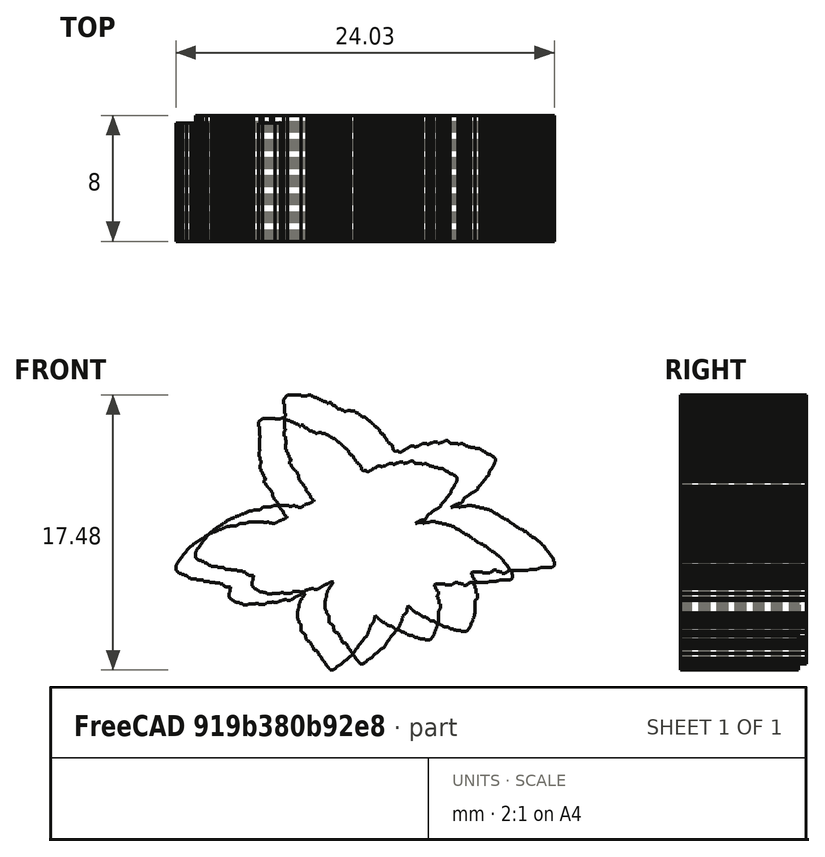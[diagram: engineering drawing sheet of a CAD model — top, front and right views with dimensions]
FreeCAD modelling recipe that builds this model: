
FCSTD DOCUMENT  (FreeCAD 1.0R39285 (Git))
Label: mintsLeafLogo_01_13_2023
License: All rights reserved
LicenseURL: http://en.wikipedia.org/wiki/All_rights_reserved
objects: Part::FeaturePython×2, Sketcher::SketchObject×1, Mesh::Feature×1, Part::Extrusion×1
note: 5 computed .brp shape members not serialized (recipe doc carries the construction recipe); baked Part::Feature solids carry a one-line shape summary decoded from their .brp

FEATURE [Sketcher::SketchObject] Sketch013
  ArcFitTolerance = 0
  FullyConstrained = false
  MakeInternals = false
  Placement = pos=(0,0,0) rot=(1,0,0;1.5708rad)
  sketch-geometry (884):
    g0: LineSegment StartX=35.7189 StartY=14.4677 StartZ=0 EndX=35.5415 EndY=14.2824 EndZ=0
    g1: LineSegment StartX=35.5415 StartY=14.2079 StartZ=0 EndX=35.4533 EndY=14.1342 EndZ=0
    g2: LineSegment StartX=35.4533 StartY=14.1342 StartZ=0 EndX=35.4583 EndY=14.0618 EndZ=0
    g3: LineSegment StartX=35.4583 StartY=14.0618 StartZ=0 EndX=35.3195 EndY=13.9216 EndZ=0
    g4: LineSegment StartX=35.3195 StartY=13.9216 StartZ=0 EndX=35.3195 EndY=13.853 EndZ=0
    g5: LineSegment StartX=35.3195 StartY=13.853 StartZ=0 EndX=35.248 EndY=13.7975 EndZ=0
    g6: LineSegment StartX=35.248 StartY=13.7975 StartZ=0 EndX=35.248 EndY=13.6573 EndZ=0
    g7: LineSegment StartX=35.248 StartY=13.6573 StartZ=0 EndX=35.1825 EndY=13.5912 EndZ=0
    g8: LineSegment StartX=35.1825 StartY=13.5912 StartZ=0 EndX=35.1825 EndY=13.2647 EndZ=0
    g9: LineSegment StartX=35.1825 StartY=13.2647 StartZ=0 EndX=35.0994 EndY=13.159 EndZ=0
    g10: LineSegment StartX=35.0994 StartY=13.159 StartZ=0 EndX=35.0994 EndY=13.0459 EndZ=0
    g11: LineSegment StartX=35.0994 StartY=13.0459 StartZ=0 EndX=35.0336 EndY=12.9565 EndZ=0
    g12: LineSegment StartX=35.0336 StartY=12.9565 StartZ=0 EndX=35.0336 EndY=12.3489 EndZ=0
    g13: LineSegment StartX=35.0336 StartY=12.3489 StartZ=0 EndX=35.1008 EndY=12.3489 EndZ=0
    g14: LineSegment StartX=35.1008 StartY=12.3489 StartZ=0 EndX=35.1008 EndY=12.2102 EndZ=0
    g15: LineSegment StartX=35.1008 StartY=12.2102 StartZ=0 EndX=35.1709 EndY=12.2072 EndZ=0
    g16: LineSegment StartX=35.1709 StartY=12.2072 StartZ=0 EndX=35.1709 EndY=11.9948 EndZ=0
    g17: LineSegment StartX=35.1709 StartY=11.9948 StartZ=0 EndX=35.2359 EndY=11.9948 EndZ=0
    g18: LineSegment StartX=35.2359 StartY=11.9948 StartZ=0 EndX=35.2359 EndY=11.9181 EndZ=0
    g19: LineSegment StartX=35.2359 StartY=11.9181 StartZ=0 EndX=35.3001 EndY=11.9181 EndZ=0
    g20: LineSegment StartX=35.3001 StartY=11.9181 StartZ=0 EndX=35.3001 EndY=11.8402 EndZ=0
    g21: LineSegment StartX=35.3001 StartY=11.8402 StartZ=0 EndX=35.3675 EndY=11.8402 EndZ=0
    g22: LineSegment StartX=35.3675 StartY=11.8402 StartZ=0 EndX=35.3675 EndY=11.2433 EndZ=0
    g23: LineSegment StartX=35.3675 StartY=11.2433 StartZ=0 EndX=35.435 EndY=11.2433 EndZ=0
    g24: LineSegment StartX=35.435 StartY=11.2433 StartZ=0 EndX=35.435 EndY=11.1727 EndZ=0
    g25: LineSegment StartX=35.435 StartY=11.1727 StartZ=0 EndX=35.5098 EndY=11.1727 EndZ=0
    g26: LineSegment StartX=35.5098 StartY=11.1727 StartZ=0 EndX=35.5098 EndY=11.1026 EndZ=0
    g27: LineSegment StartX=35.5098 StartY=11.1026 StartZ=0 EndX=35.6558 EndY=11.1026 EndZ=0
    g28: LineSegment StartX=35.6558 StartY=11.1026 StartZ=0 EndX=35.6558 EndY=11.0252 EndZ=0
    g29: LineSegment StartX=35.6558 StartY=11.0252 StartZ=0 EndX=35.7128 EndY=11.0252 EndZ=0
    g30: LineSegment StartX=35.7128 StartY=11.0252 StartZ=0 EndX=35.7128 EndY=10.7682 EndZ=0
    g31: LineSegment StartX=35.7128 StartY=10.7682 StartZ=0 EndX=35.7756 EndY=10.7681 EndZ=0
    g32: LineSegment StartX=35.7756 StartY=10.7681 StartZ=0 EndX=35.7756 EndY=10.5644 EndZ=0
    g33: LineSegment StartX=35.7756 StartY=10.5644 StartZ=0 EndX=35.846 EndY=10.5644 EndZ=0
    g34: LineSegment StartX=35.846 StartY=10.5644 StartZ=0 EndX=35.846 EndY=10.4767 EndZ=0
    g35: LineSegment StartX=35.846 StartY=10.4767 StartZ=0 EndX=35.988 EndY=10.4767 EndZ=0
    g36: LineSegment StartX=35.988 StartY=10.4767 StartZ=0 EndX=35.988 EndY=10.4228 EndZ=0
    g37: LineSegment StartX=35.988 StartY=10.4228 StartZ=0 EndX=36.1201 EndY=10.4228 EndZ=0
    g38: LineSegment StartX=36.1201 StartY=10.4228 StartZ=0 EndX=36.1201 EndY=10.2907 EndZ=0
    g39: LineSegment StartX=36.1201 StartY=10.2907 StartZ=0 EndX=36.1926 EndY=10.2907 EndZ=0
    g40: LineSegment StartX=36.1926 StartY=10.2907 StartZ=0 EndX=36.1926 EndY=10.1585 EndZ=0
    g41: LineSegment StartX=36.1926 StartY=10.1585 StartZ=0 EndX=36.2533 EndY=10.1585 EndZ=0
    g42: LineSegment StartX=36.2533 StartY=10.1585 StartZ=0 EndX=36.2533 EndY=10.0897 EndZ=0
    g43: LineSegment StartX=36.2533 StartY=10.0897 StartZ=0 EndX=36.3179 EndY=10.0897 EndZ=0
    g44: LineSegment StartX=36.3179 StartY=10.0897 StartZ=0 EndX=36.3179 EndY=9.8871 EndZ=0
    g45: LineSegment StartX=36.3179 StartY=9.8871 StartZ=0 EndX=36.3888 EndY=9.8871 EndZ=0
    g46: LineSegment StartX=36.3888 StartY=9.8871 StartZ=0 EndX=36.3888 EndY=9.73503 EndZ=0
    g47: LineSegment StartX=36.3888 StartY=9.73503 StartZ=0 EndX=36.4516 EndY=9.73503 EndZ=0
    g48: LineSegment StartX=36.4516 StartY=9.73503 StartZ=0 EndX=36.4516 EndY=9.65617 EndZ=0
    g49: LineSegment StartX=36.4516 StartY=9.65617 StartZ=0 EndX=36.6707 EndY=9.65617 EndZ=0
    g50: LineSegment StartX=36.6707 StartY=9.65617 StartZ=0 EndX=36.6707 EndY=9.58899 EndZ=0
    g51: LineSegment StartX=36.6707 StartY=9.58899 StartZ=0 EndX=36.7335 EndY=9.58899 EndZ=0
    g52: LineSegment StartX=36.7335 StartY=9.58899 StartZ=0 EndX=36.7335 EndY=9.51158 EndZ=0
    g53: LineSegment StartX=36.7335 StartY=9.51158 StartZ=0 EndX=36.7948 EndY=9.51158 EndZ=0
    g54: LineSegment StartX=36.7948 StartY=9.51158 StartZ=0 EndX=36.7948 EndY=9.40351 EndZ=0
    g55: LineSegment StartX=36.7948 StartY=9.40351 StartZ=0 EndX=36.8664 EndY=9.40351 EndZ=0
    g56: LineSegment StartX=36.8664 StartY=9.40351 StartZ=0 EndX=36.8664 EndY=9.2487 EndZ=0
    g57: LineSegment StartX=36.8664 StartY=9.2487 StartZ=0 EndX=36.9292 EndY=9.2487 EndZ=0
    g58: LineSegment StartX=36.9292 StartY=9.2487 StartZ=0 EndX=36.9292 EndY=9.18298 EndZ=0
    g59: LineSegment StartX=36.9292 StartY=9.18298 StartZ=0 EndX=37.0036 EndY=9.18298 EndZ=0
    g60: LineSegment StartX=37.0036 StartY=9.18298 StartZ=0 EndX=37.0036 EndY=9.12121 EndZ=0
    g61: LineSegment StartX=37.0036 StartY=9.12121 StartZ=0 EndX=37.066 EndY=9.12121 EndZ=0
    g62: LineSegment StartX=37.066 StartY=9.12121 StartZ=0 EndX=37.066 EndY=8.98122 EndZ=0
    g63: LineSegment StartX=37.066 StartY=8.98122 StartZ=0 EndX=37.1365 EndY=8.98122 EndZ=0
    g64: LineSegment StartX=37.1365 StartY=8.98122 StartZ=0 EndX=37.1365 EndY=8.85617 EndZ=0
    g65: LineSegment StartX=37.1365 StartY=8.85617 StartZ=0 EndX=37.2117 EndY=8.85617 EndZ=0
    g66: LineSegment StartX=37.2117 StartY=8.85617 StartZ=0 EndX=37.2117 EndY=8.77808 EndZ=0
    g67: LineSegment StartX=37.2117 StartY=8.77808 StartZ=0 EndX=37.276 EndY=8.7779 EndZ=0
    g68: LineSegment StartX=37.276 StartY=8.7779 StartZ=0 EndX=37.276 EndY=8.70839 EndZ=0
    g69: LineSegment StartX=37.276 StartY=8.70839 StartZ=0 EndX=37.3475 EndY=8.70839 EndZ=0
    g70: LineSegment StartX=37.3475 StartY=8.70839 StartZ=0 EndX=37.3475 EndY=8.58602 EndZ=0
    g71: LineSegment StartX=37.3475 StartY=8.58602 StartZ=0 EndX=37.4111 EndY=8.58602 EndZ=0
    g72: LineSegment StartX=37.4111 StartY=8.58602 StartZ=0 EndX=37.4111 EndY=8.50272 EndZ=0
    g73: LineSegment StartX=37.4111 StartY=8.50272 StartZ=0 EndX=37.4778 EndY=8.50272 EndZ=0
    g74: LineSegment StartX=37.4778 StartY=8.50272 StartZ=0 EndX=37.4778 EndY=8.37852 EndZ=0
    g75: LineSegment StartX=37.4778 StartY=8.37852 StartZ=0 EndX=37.55 EndY=8.37852 EndZ=0
    g76: LineSegment StartX=37.55 StartY=8.37852 StartZ=0 EndX=37.55 EndY=8.29594 EndZ=0
    g77: LineSegment StartX=37.55 StartY=8.29594 StartZ=0 EndX=37.6238 EndY=8.29594 EndZ=0
    g78: LineSegment StartX=37.6238 StartY=8.29594 StartZ=0 EndX=37.6238 EndY=8.20831 EndZ=0
    g79: LineSegment StartX=37.6238 StartY=8.20831 StartZ=0 EndX=37.6953 EndY=8.21123 EndZ=0
    g80: LineSegment StartX=37.6953 StartY=8.21123 StartZ=0 EndX=37.6953 EndY=8.14022 EndZ=0
    g81: LineSegment StartX=37.6953 StartY=8.14022 StartZ=0 EndX=37.7536 EndY=8.14414 EndZ=0
    g82: LineSegment StartX=37.7536 StartY=8.14414 StartZ=0 EndX=37.7574 EndY=8.06459 EndZ=0
    g83: LineSegment StartX=37.7574 StartY=8.06459 StartZ=0 EndX=37.8181 EndY=8.06459 EndZ=0
    g84: LineSegment StartX=37.8181 StartY=8.06459 StartZ=0 EndX=37.8216 EndY=7.98967 EndZ=0
    g85: LineSegment StartX=37.8216 StartY=7.98967 StartZ=0 EndX=38.1025 EndY=7.98967 EndZ=0
    g86: LineSegment StartX=38.1025 StartY=7.98967 StartZ=0 EndX=38.1917 EndY=8.08042 EndZ=0
    g87: LineSegment StartX=38.1917 StartY=8.08042 StartZ=0 EndX=38.2417 EndY=8.08577 EndZ=0
    g88: LineSegment StartX=38.2417 StartY=8.08577 StartZ=0 EndX=38.4557 EndY=8.32302 EndZ=0
    g89: LineSegment StartX=38.4557 StartY=8.32302 StartZ=0 EndX=38.5235 EndY=8.32302 EndZ=0
    g90: LineSegment StartX=38.5235 StartY=8.32302 StartZ=0 EndX=38.5887 EndY=8.40314 EndZ=0
    g91: LineSegment StartX=38.5887 StartY=8.40314 StartZ=0 EndX=38.6773 EndY=8.40314 EndZ=0
    g92: LineSegment StartX=38.6773 StartY=8.40314 StartZ=0 EndX=39.0643 EndY=8.80818 EndZ=0
    g93: LineSegment StartX=39.0643 StartY=8.80818 StartZ=0 EndX=39.152 EndY=8.80818 EndZ=0
    g94: LineSegment StartX=39.152 StartY=8.80818 StartZ=0 EndX=39.5355 EndY=9.19803 EndZ=0
    g95: LineSegment StartX=39.5355 StartY=9.19803 StartZ=0 EndX=39.6318 EndY=9.19803 EndZ=0
    g96: LineSegment StartX=39.6318 StartY=9.19803 StartZ=0 EndX=39.792 EndY=9.38195 EndZ=0
    g97: LineSegment StartX=39.792 StartY=9.38195 StartZ=0 EndX=39.7884 EndY=9.45608 EndZ=0
    g98: LineSegment StartX=39.7884 StartY=9.45608 StartZ=0 EndX=39.9772 EndY=9.63446 EndZ=0
    g99: LineSegment StartX=39.9772 StartY=9.63446 StartZ=0 EndX=39.9772 EndY=9.72533 EndZ=0
    g100: LineSegment StartX=39.9772 StartY=9.72533 StartZ=0 EndX=40.1697 EndY=9.91904 EndZ=0
    g101: LineSegment StartX=40.1697 StartY=9.91904 StartZ=0 EndX=40.1746 EndY=9.99558 EndZ=0
    g102: LineSegment StartX=40.1746 StartY=9.99558 StartZ=0 EndX=40.2388 EndY=10.0603 EndZ=0
    g103: LineSegment StartX=40.2388 StartY=10.0603 StartZ=0 EndX=40.2423 EndY=10.1261 EndZ=0
    g104: LineSegment StartX=40.2423 StartY=10.1261 StartZ=0 EndX=40.5948 EndY=10.4793 EndZ=0
    g105: LineSegment StartX=40.5948 StartY=10.4793 StartZ=0 EndX=40.5948 EndY=10.5499 EndZ=0
    g106: LineSegment StartX=40.5948 StartY=10.5499 StartZ=0 EndX=40.6701 EndY=10.618 EndZ=0
    g107: LineSegment StartX=40.6701 StartY=10.618 StartZ=0 EndX=40.6581 EndY=10.6527 EndZ=0
    g108: LineSegment StartX=40.6581 StartY=10.6527 StartZ=0 EndX=40.6988 EndY=10.6527 EndZ=0
    g109: LineSegment StartX=40.6988 StartY=10.6527 StartZ=0 EndX=40.9317 EndY=10.8877 EndZ=0
    g110: LineSegment StartX=40.9317 StartY=10.8877 StartZ=0 EndX=40.9317 EndY=10.9592 EndZ=0
    g111: LineSegment StartX=40.9317 StartY=10.9592 StartZ=0 EndX=41.0136 EndY=11.0405 EndZ=0
    g112: LineSegment StartX=41.0136 StartY=11.0405 StartZ=0 EndX=41.0068 EndY=11.1648 EndZ=0
    g113: LineSegment StartX=41.0068 StartY=11.1648 StartZ=0 EndX=41.0763 EndY=11.2275 EndZ=0
    g114: LineSegment StartX=41.0763 StartY=11.2275 StartZ=0 EndX=41.0723 EndY=11.2979 EndZ=0
    g115: LineSegment StartX=41.0723 StartY=11.2979 StartZ=0 EndX=41.15 EndY=11.3821 EndZ=0
    g116: LineSegment StartX=41.15 StartY=11.3821 StartZ=0 EndX=41.15 EndY=11.5724 EndZ=0
    g117: LineSegment StartX=41.15 StartY=11.5724 StartZ=0 EndX=41.2317 EndY=11.6351 EndZ=0
    g118: LineSegment StartX=41.2317 StartY=11.6351 StartZ=0 EndX=41.2155 EndY=11.7717 EndZ=0
    g119: LineSegment StartX=41.2155 StartY=11.7717 StartZ=0 EndX=41.2837 EndY=11.8432 EndZ=0
    g120: LineSegment StartX=41.2837 StartY=11.8432 StartZ=0 EndX=41.2786 EndY=11.8698 EndZ=0
    g121: LineSegment StartX=41.2786 StartY=11.8698 StartZ=0 EndX=41.3138 EndY=11.8698 EndZ=0
    g122: LineSegment StartX=41.3138 StartY=11.8698 StartZ=0 EndX=41.5455 EndY=12.1045 EndZ=0
    g123: LineSegment StartX=41.5455 StartY=12.1045 StartZ=0 EndX=41.5618 EndY=12.4305 EndZ=0
    g124: LineSegment StartX=41.5618 StartY=12.4305 StartZ=0 EndX=41.6277 EndY=12.505 EndZ=0
    g125: LineSegment StartX=41.6277 StartY=12.505 StartZ=0 EndX=41.6277 EndY=12.6108 EndZ=0
    g126: LineSegment StartX=41.6277 StartY=12.6108 StartZ=0 EndX=41.692 EndY=12.5393 EndZ=0
    g127: LineSegment StartX=41.692 StartY=12.5393 StartZ=0 EndX=41.7679 EndY=12.5393 EndZ=0
    g128: LineSegment StartX=41.7679 StartY=12.5393 StartZ=0 EndX=41.7679 EndY=12.4516 EndZ=0
    g129: LineSegment StartX=41.7679 StartY=12.4516 StartZ=0 EndX=41.8336 EndY=12.4546 EndZ=0
    g130: LineSegment StartX=41.8336 StartY=12.4546 StartZ=0 EndX=41.8336 EndY=12.3903 EndZ=0
    g131: LineSegment StartX=41.8336 StartY=12.3903 StartZ=0 EndX=41.8935 EndY=12.3903 EndZ=0
    g132: LineSegment StartX=41.8935 StartY=12.3903 StartZ=0 EndX=41.8935 EndY=12.3173 EndZ=0
    g133: LineSegment StartX=41.8935 StartY=12.3173 StartZ=0 EndX=41.9592 EndY=12.3217 EndZ=0
    g134: LineSegment StartX=41.9592 StartY=12.3217 StartZ=0 EndX=41.9651 EndY=12.2501 EndZ=0
    g135: LineSegment StartX=41.9651 StartY=12.2501 StartZ=0 EndX=42.0235 EndY=12.2559 EndZ=0
    g136: LineSegment StartX=42.0235 StartY=12.2559 StartZ=0 EndX=42.0264 EndY=12.1829 EndZ=0
    g137: LineSegment StartX=42.0264 StartY=12.1829 StartZ=0 EndX=42.1067 EndY=12.1888 EndZ=0
    g138: LineSegment StartX=42.1067 StartY=12.1888 StartZ=0 EndX=42.1067 EndY=12.1143 EndZ=0
    g139: LineSegment StartX=42.1067 StartY=12.1143 StartZ=0 EndX=42.2426 EndY=12.1216 EndZ=0
    g140: LineSegment StartX=42.2426 StartY=12.1216 StartZ=0 EndX=42.2426 EndY=12.0413 EndZ=0
    g141: LineSegment StartX=42.2426 StartY=12.0413 StartZ=0 EndX=42.4427 EndY=12.0413 EndZ=0
    g142: LineSegment StartX=42.4427 StartY=12.0413 StartZ=0 EndX=42.45 EndY=11.9566 EndZ=0
    g143: LineSegment StartX=42.45 StartY=11.9566 StartZ=0 EndX=42.523 EndY=11.9639 EndZ=0
    g144: LineSegment StartX=42.523 StartY=11.9639 StartZ=0 EndX=42.5274 EndY=11.8952 EndZ=0
    g145: LineSegment StartX=42.5274 StartY=11.8952 StartZ=0 EndX=42.5931 EndY=11.9011 EndZ=0
    g146: LineSegment StartX=42.5931 StartY=11.9011 StartZ=0 EndX=42.5931 EndY=11.847 EndZ=0
    g147: LineSegment StartX=42.5931 StartY=11.847 StartZ=0 EndX=42.6457 EndY=11.8499 EndZ=0
    g148: LineSegment StartX=42.6457 StartY=11.8499 StartZ=0 EndX=42.6457 EndY=11.7886 EndZ=0
    g149: LineSegment StartX=42.6457 StartY=11.7886 StartZ=0 EndX=42.7844 EndY=11.7886 EndZ=0
    g150: LineSegment StartX=42.7844 StartY=11.7886 StartZ=0 EndX=42.7844 EndY=11.7131 EndZ=0
    g151: LineSegment StartX=42.7844 StartY=11.7131 StartZ=0 EndX=43.0642 EndY=11.7131 EndZ=0
    g152: LineSegment StartX=43.0642 StartY=11.7131 StartZ=0 EndX=43.0642 EndY=11.6357 EndZ=0
    g153: LineSegment StartX=43.0642 StartY=11.6357 StartZ=0 EndX=43.1985 EndY=11.6357 EndZ=0
    g154: LineSegment StartX=43.1985 StartY=11.6357 StartZ=0 EndX=43.1985 EndY=11.5714 EndZ=0
    g155: LineSegment StartX=43.1985 StartY=11.5714 StartZ=0 EndX=43.2613 EndY=11.5714 EndZ=0
    g156: LineSegment StartX=43.2613 StartY=11.5714 StartZ=0 EndX=43.2613 EndY=11.5086 EndZ=0
    g157: LineSegment StartX=43.2613 StartY=11.5086 StartZ=0 EndX=43.3285 EndY=11.5086 EndZ=0
    g158: LineSegment StartX=43.3285 StartY=11.5086 StartZ=0 EndX=43.3285 EndY=11.4327 EndZ=0
    g159: LineSegment StartX=43.3285 StartY=11.4327 StartZ=0 EndX=43.3913 EndY=11.4371 EndZ=0
    g160: LineSegment StartX=43.3913 StartY=11.4371 StartZ=0 EndX=43.3932 EndY=11.3717 EndZ=0
    g161: LineSegment StartX=43.3932 StartY=11.3717 StartZ=0 EndX=43.7436 EndY=11.3717 EndZ=0
    g162: LineSegment StartX=43.7436 StartY=11.3717 StartZ=0 EndX=43.7436 EndY=11.3021 EndZ=0
    g163: LineSegment StartX=43.7436 StartY=11.3021 StartZ=0 EndX=43.8098 EndY=11.3021 EndZ=0
    g164: LineSegment StartX=43.8098 StartY=11.3021 StartZ=0 EndX=43.8134 EndY=11.2285 EndZ=0
    g165: LineSegment StartX=43.8134 StartY=11.2285 StartZ=0 EndX=44.0238 EndY=11.2285 EndZ=0
    g166: LineSegment StartX=44.0238 StartY=11.2285 StartZ=0 EndX=44.0238 EndY=11.1603 EndZ=0
    g167: LineSegment StartX=44.0238 StartY=11.1603 StartZ=0 EndX=44.1542 EndY=11.1603 EndZ=0
    g168: LineSegment StartX=44.1542 StartY=11.1603 StartZ=0 EndX=44.1506 EndY=11.0922 EndZ=0
    g169: LineSegment StartX=44.1506 StartY=11.0922 StartZ=0 EndX=44.2845 EndY=11.1005 EndZ=0
    g170: LineSegment StartX=44.2845 StartY=11.1005 StartZ=0 EndX=44.2845 EndY=11.0276 EndZ=0
    g171: LineSegment StartX=44.2845 StartY=11.0276 StartZ=0 EndX=44.3538 EndY=11.0312 EndZ=0
    g172: LineSegment StartX=44.3538 StartY=11.0312 StartZ=0 EndX=44.3538 EndY=10.9534 EndZ=0
    g173: LineSegment StartX=44.3538 StartY=10.9534 StartZ=0 EndX=44.4925 EndY=10.9534 EndZ=0
    g174: LineSegment StartX=44.4925 StartY=10.9534 StartZ=0 EndX=44.4925 EndY=10.9066 EndZ=0
    g175: LineSegment StartX=44.4925 StartY=10.9066 StartZ=0 EndX=44.8405 EndY=10.9066 EndZ=0
    g176: LineSegment StartX=44.8405 StartY=10.9066 StartZ=0 EndX=44.8405 EndY=10.8227 EndZ=0
    g177: LineSegment StartX=44.8405 StartY=10.8227 StartZ=0 EndX=44.9671 EndY=10.8245 EndZ=0
    g178: LineSegment StartX=44.9671 StartY=10.8245 StartZ=0 EndX=44.9671 EndY=10.7496 EndZ=0
    g179: LineSegment StartX=44.9671 StartY=10.7496 StartZ=0 EndX=45.2382 EndY=10.7496 EndZ=0
    g180: LineSegment StartX=45.2382 StartY=10.7496 StartZ=0 EndX=45.2382 EndY=10.6783 EndZ=0
    g181: LineSegment StartX=45.2382 StartY=10.6783 StartZ=0 EndX=45.438 EndY=10.6783 EndZ=0
    g182: LineSegment StartX=45.438 StartY=10.6783 StartZ=0 EndX=45.438 EndY=10.6176 EndZ=0
    g183: LineSegment StartX=45.438 StartY=10.6176 StartZ=0 EndX=45.8572 EndY=10.6176 EndZ=0
    g184: LineSegment StartX=45.8572 StartY=10.6176 StartZ=0 EndX=45.8572 EndY=10.548 EndZ=0
    g185: LineSegment StartX=45.8572 StartY=10.548 StartZ=0 EndX=46.2711 EndY=10.548 EndZ=0
    g186: LineSegment StartX=46.2711 StartY=10.548 StartZ=0 EndX=46.5712 EndY=10.876 EndZ=0
    g187: LineSegment StartX=46.5712 StartY=10.876 StartZ=0 EndX=46.568 EndY=10.9537 EndZ=0
    g188: LineSegment StartX=46.568 StartY=10.9537 StartZ=0 EndX=46.6513 EndY=11.0387 EndZ=0
    g189: LineSegment StartX=46.6513 StartY=11.0387 StartZ=0 EndX=46.6513 EndY=11.2162 EndZ=0
    g190: LineSegment StartX=46.6513 StartY=11.2162 StartZ=0 EndX=46.7535 EndY=11.317 EndZ=0
    g191: LineSegment StartX=46.7535 StartY=11.317 StartZ=0 EndX=46.7462 EndY=11.4353 EndZ=0
    g192: LineSegment StartX=46.7462 StartY=11.4353 StartZ=0 EndX=46.8178 EndY=11.5141 EndZ=0
    g193: LineSegment StartX=46.8178 StartY=11.5141 StartZ=0 EndX=46.8081 EndY=11.636 EndZ=0
    g194: LineSegment StartX=46.8081 StartY=11.636 StartZ=0 EndX=46.8919 EndY=11.7287 EndZ=0
    g195: LineSegment StartX=46.8919 StartY=11.7287 StartZ=0 EndX=46.8919 EndY=11.9142 EndZ=0
    g196: LineSegment StartX=46.8919 StartY=11.9142 StartZ=0 EndX=46.9704 EndY=12.0106 EndZ=0
    g197: LineSegment StartX=46.9704 StartY=12.0106 StartZ=0 EndX=46.9704 EndY=13.0147 EndZ=0
    g198: LineSegment StartX=46.9704 StartY=13.0147 StartZ=0 EndX=47.1435 EndY=13.1957 EndZ=0
    g199: LineSegment StartX=47.1435 StartY=13.1957 StartZ=0 EndX=47.1435 EndY=13.5812 EndZ=0
    g200: LineSegment StartX=47.1435 StartY=13.5812 StartZ=0 EndX=47.0232 EndY=13.5812 EndZ=0
    g201: LineSegment StartX=47.0232 StartY=13.5812 StartZ=0 EndX=47.0232 EndY=13.968 EndZ=0
    g202: LineSegment StartX=47.0232 StartY=13.968 StartZ=0 EndX=46.9387 EndY=13.981 EndZ=0
    g203: LineSegment StartX=46.9387 StartY=13.981 StartZ=0 EndX=46.9387 EndY=14.1923 EndZ=0
    g204: LineSegment StartX=46.9387 StartY=14.1923 StartZ=0 EndX=46.8607 EndY=14.189 EndZ=0
    g205: LineSegment StartX=46.8607 StartY=14.189 StartZ=0 EndX=46.8607 EndY=14.2768 EndZ=0
    g206: LineSegment StartX=46.8607 StartY=14.2768 StartZ=0 EndX=46.9745 EndY=14.4003 EndZ=0
    g207: LineSegment StartX=46.9745 StartY=14.4003 StartZ=0 EndX=46.9842 EndY=14.6473 EndZ=0
    g208: LineSegment StartX=46.9842 StartY=14.6473 StartZ=0 EndX=46.8672 EndY=14.6603 EndZ=0
    g209: LineSegment StartX=46.8672 StartY=14.6603 StartZ=0 EndX=46.8672 EndY=14.8066 EndZ=0
    g210: LineSegment StartX=46.8672 StartY=14.8066 StartZ=0 EndX=46.799 EndY=14.8131 EndZ=0
    g211: LineSegment StartX=46.799 StartY=14.8131 StartZ=0 EndX=46.7957 EndY=14.8846 EndZ=0
    g212: LineSegment StartX=46.7957 StartY=14.8846 StartZ=0 EndX=46.7372 EndY=14.8911 EndZ=0
    g213: LineSegment StartX=46.7372 StartY=14.8911 StartZ=0 EndX=46.7502 EndY=15.0699 EndZ=0
    g214: LineSegment StartX=46.7502 StartY=15.0699 StartZ=0 EndX=46.6592 EndY=15.0764 EndZ=0
    g215: LineSegment StartX=46.6592 StartY=15.0764 StartZ=0 EndX=46.6592 EndY=15.2096 EndZ=0
    g216: LineSegment StartX=46.6592 StartY=15.2096 StartZ=0 EndX=46.7535 EndY=15.2811 EndZ=0
    g217: LineSegment StartX=46.7535 StartY=15.2811 StartZ=0 EndX=47.5498 EndY=15.2811 EndZ=0
    g218: LineSegment StartX=47.5498 StartY=15.2811 StartZ=0 EndX=47.5498 EndY=15.2015 EndZ=0
    g219: LineSegment StartX=47.5498 StartY=15.2015 StartZ=0 EndX=48.1326 EndY=15.2015 EndZ=0
    g220: LineSegment StartX=48.1326 StartY=15.2015 StartZ=0 EndX=48.1915 EndY=15.2887 EndZ=0
    g221: LineSegment StartX=48.1915 StartY=15.2887 StartZ=0 EndX=48.2811 EndY=15.2887 EndZ=0
    g222: LineSegment StartX=48.2811 StartY=15.2887 StartZ=0 EndX=48.4046 EndY=15.4194 EndZ=0
    g223: LineSegment StartX=48.4046 StartY=15.4194 StartZ=0 EndX=48.6512 EndY=15.4194 EndZ=0
    g224: LineSegment StartX=48.6512 StartY=15.4194 StartZ=0 EndX=48.6512 EndY=15.3322 EndZ=0
    g225: LineSegment StartX=48.6512 StartY=15.3322 StartZ=0 EndX=48.9084 EndY=15.3322 EndZ=0
    g226: LineSegment StartX=48.9084 StartY=15.3322 StartZ=0 EndX=48.9084 EndY=15.2647 EndZ=0
    g227: LineSegment StartX=48.9084 StartY=15.2647 StartZ=0 EndX=49.1131 EndY=15.2647 EndZ=0
    g228: LineSegment StartX=49.1131 StartY=15.2647 StartZ=0 EndX=49.1131 EndY=15.171 EndZ=0
    g229: LineSegment StartX=49.1131 StartY=15.171 StartZ=0 EndX=49.344 EndY=15.171 EndZ=0
    g230: LineSegment StartX=49.344 StartY=15.171 StartZ=0 EndX=49.4317 EndY=15.2779 EndZ=0
    g231: LineSegment StartX=49.4317 StartY=15.2779 StartZ=0 EndX=49.513 EndY=15.2714 EndZ=0
    g232: LineSegment StartX=49.513 StartY=15.2714 StartZ=0 EndX=49.6365 EndY=15.4177 EndZ=0
    g233: LineSegment StartX=49.6365 StartY=15.4177 StartZ=0 EndX=51.1609 EndY=15.4177 EndZ=0
    g234: LineSegment StartX=51.1609 StartY=15.4177 StartZ=0 EndX=51.2713 EndY=15.4747 EndZ=0
    g235: LineSegment StartX=51.2713 StartY=15.4747 StartZ=0 EndX=51.8707 EndY=15.4747 EndZ=0
    g236: LineSegment StartX=51.8707 StartY=15.4747 StartZ=0 EndX=51.9501 EndY=15.5501 EndZ=0
    g237: LineSegment StartX=51.9501 StartY=15.5501 StartZ=0 EndX=52.0613 EndY=15.5501 EndZ=0
    g238: LineSegment StartX=52.0613 StartY=15.5501 StartZ=0 EndX=52.1566 EndY=15.6335 EndZ=0
    g239: LineSegment StartX=52.1566 StartY=15.6335 StartZ=0 EndX=53.0776 EndY=15.6335 EndZ=0
    g240: LineSegment StartX=53.0776 StartY=15.6335 StartZ=0 EndX=53.2557 EndY=15.8082 EndZ=0
    g241: LineSegment StartX=53.2557 StartY=15.8082 StartZ=0 EndX=53.2557 EndY=16.103 EndZ=0
    g242: LineSegment StartX=53.2557 StartY=16.103 StartZ=0 EndX=53.1958 EndY=16.103 EndZ=0
    g243: LineSegment StartX=53.1958 StartY=16.103 StartZ=0 EndX=53.1958 EndY=16.3046 EndZ=0
    g244: LineSegment StartX=53.1958 StartY=16.3046 StartZ=0 EndX=53.1301 EndY=16.3017 EndZ=0
    g245: LineSegment StartX=53.1301 StartY=16.3017 StartZ=0 EndX=53.1301 EndY=16.4404 EndZ=0
    g246: LineSegment StartX=53.1301 StartY=16.4404 StartZ=0 EndX=53.0594 EndY=16.4404 EndZ=0
    g247: LineSegment StartX=53.0594 StartY=16.4404 StartZ=0 EndX=53.0558 EndY=16.5171 EndZ=0
    g248: LineSegment StartX=53.0558 StartY=16.5171 StartZ=0 EndX=52.9773 EndY=16.5171 EndZ=0
    g249: LineSegment StartX=52.9773 StartY=16.5171 StartZ=0 EndX=52.9773 EndY=16.6455 EndZ=0
    g250: LineSegment StartX=52.9773 StartY=16.6455 StartZ=0 EndX=52.9219 EndY=16.6452 EndZ=0
    g251: LineSegment StartX=52.9219 StartY=16.6452 StartZ=0 EndX=52.9219 EndY=16.7146 EndZ=0
    g252: LineSegment StartX=52.9219 StartY=16.7146 StartZ=0 EndX=52.8549 EndY=16.7146 EndZ=0
    g253: LineSegment StartX=52.8549 StartY=16.7146 StartZ=0 EndX=52.8535 EndY=16.7863 EndZ=0
    g254: LineSegment StartX=52.8535 StartY=16.7863 StartZ=0 EndX=52.7868 EndY=16.7863 EndZ=0
    g255: LineSegment StartX=52.7868 StartY=16.7863 StartZ=0 EndX=52.7868 EndY=16.9211 EndZ=0
    g256: LineSegment StartX=52.7868 StartY=16.9211 StartZ=0 EndX=52.715 EndY=16.9211 EndZ=0
    g257: LineSegment StartX=52.715 StartY=16.9211 StartZ=0 EndX=52.715 EndY=16.98 EndZ=0
    g258: LineSegment StartX=52.715 StartY=16.98 StartZ=0 EndX=52.6457 EndY=16.98 EndZ=0
    g259: LineSegment StartX=52.6457 StartY=16.98 StartZ=0 EndX=52.6457 EndY=17.0366 EndZ=0
    g260: LineSegment StartX=52.6457 StartY=17.0366 StartZ=0 EndX=52.5763 EndY=17.0366 EndZ=0
    g261: LineSegment StartX=52.5763 StartY=17.0366 StartZ=0 EndX=52.5763 EndY=17.128 EndZ=0
    g262: LineSegment StartX=52.5763 StartY=17.128 StartZ=0 EndX=52.5147 EndY=17.128 EndZ=0
    g263: LineSegment StartX=52.5147 StartY=17.128 StartZ=0 EndX=52.5147 EndY=17.2695 EndZ=0
    g264: LineSegment StartX=52.5147 StartY=17.2695 StartZ=0 EndX=52.4502 EndY=17.2647 EndZ=0
    g265: LineSegment StartX=52.4502 StartY=17.2647 StartZ=0 EndX=52.4454 EndY=17.336 EndZ=0
    g266: LineSegment StartX=52.4454 StartY=17.336 StartZ=0 EndX=52.3797 EndY=17.3384 EndZ=0
    g267: LineSegment StartX=52.3797 StartY=17.3384 StartZ=0 EndX=52.3829 EndY=17.4058 EndZ=0
    g268: LineSegment StartX=52.3829 StartY=17.4058 StartZ=0 EndX=52.318 EndY=17.4026 EndZ=0
    g269: LineSegment StartX=52.318 StartY=17.4026 StartZ=0 EndX=52.318 EndY=17.4715 EndZ=0
    g270: LineSegment StartX=52.318 StartY=17.4715 StartZ=0 EndX=52.2451 EndY=17.4715 EndZ=0
    g271: LineSegment StartX=52.2451 StartY=17.4715 StartZ=0 EndX=52.2451 EndY=17.5364 EndZ=0
    g272: LineSegment StartX=52.2451 StartY=17.5364 StartZ=0 EndX=52.1833 EndY=17.5388 EndZ=0
    g273: LineSegment StartX=52.1833 StartY=17.5388 StartZ=0 EndX=52.1833 EndY=17.6077 EndZ=0
    g274: LineSegment StartX=52.1833 StartY=17.6077 StartZ=0 EndX=52.1144 EndY=17.6077 EndZ=0
    g275: LineSegment StartX=52.1144 StartY=17.6077 StartZ=0 EndX=52.1144 EndY=17.6741 EndZ=0
    g276: LineSegment StartX=52.1144 StartY=17.6741 StartZ=0 EndX=52.0495 EndY=17.6741 EndZ=0
    g277: LineSegment StartX=52.0495 StartY=17.6741 StartZ=0 EndX=52.0495 EndY=17.7495 EndZ=0
    g278: LineSegment StartX=52.0495 StartY=17.7495 StartZ=0 EndX=51.9017 EndY=17.7495 EndZ=0
    g279: LineSegment StartX=51.9017 StartY=17.7495 StartZ=0 EndX=51.9017 EndY=17.8092 EndZ=0
    g280: LineSegment StartX=51.9017 StartY=17.8092 StartZ=0 EndX=51.8351 EndY=17.8092 EndZ=0
    g281: LineSegment StartX=51.8351 StartY=17.8092 StartZ=0 EndX=51.8351 EndY=17.8911 EndZ=0
    g282: LineSegment StartX=51.8351 StartY=17.8911 StartZ=0 EndX=51.7639 EndY=17.8911 EndZ=0
    g283: LineSegment StartX=51.7639 StartY=17.8911 StartZ=0 EndX=51.7639 EndY=17.9626 EndZ=0
    g284: LineSegment StartX=51.7639 StartY=17.9626 StartZ=0 EndX=51.6325 EndY=17.9626 EndZ=0
    g285: LineSegment StartX=51.6325 StartY=17.9626 StartZ=0 EndX=51.6325 EndY=18.0284 EndZ=0
    g286: LineSegment StartX=51.6325 StartY=18.0284 StartZ=0 EndX=51.485 EndY=18.0284 EndZ=0
    g287: LineSegment StartX=51.485 StartY=18.0284 StartZ=0 EndX=51.485 EndY=18.0711 EndZ=0
    g288: LineSegment StartX=51.485 StartY=18.0711 StartZ=0 EndX=51.4163 EndY=18.0711 EndZ=0
    g289: LineSegment StartX=51.4163 StartY=18.0711 StartZ=0 EndX=51.4163 EndY=18.1587 EndZ=0
    g290: LineSegment StartX=51.4163 StartY=18.1587 StartZ=0 EndX=51.2878 EndY=18.1587 EndZ=0
    g291: LineSegment StartX=51.2878 StartY=18.1587 StartZ=0 EndX=51.2878 EndY=18.2275 EndZ=0
    g292: LineSegment StartX=51.2878 StartY=18.2275 StartZ=0 EndX=51.2232 EndY=18.2275 EndZ=0
    g293: LineSegment StartX=51.2232 StartY=18.2275 StartZ=0 EndX=51.2267 EndY=18.2921 EndZ=0
    g294: LineSegment StartX=51.2267 StartY=18.2921 StartZ=0 EndX=51.1526 EndY=18.2921 EndZ=0
    g295: LineSegment StartX=51.1526 StartY=18.2921 StartZ=0 EndX=51.1526 EndY=18.3662 EndZ=0
    g296: LineSegment StartX=51.1526 StartY=18.3662 StartZ=0 EndX=51.0845 EndY=18.3602 EndZ=0
    g297: LineSegment StartX=51.0845 StartY=18.3602 StartZ=0 EndX=51.0845 EndY=18.4424 EndZ=0
    g298: LineSegment StartX=51.0845 StartY=18.4424 StartZ=0 EndX=51.0222 EndY=18.4424 EndZ=0
    g299: LineSegment StartX=51.0222 StartY=18.4424 StartZ=0 EndX=51.0222 EndY=18.5138 EndZ=0
    g300: LineSegment StartX=51.0222 StartY=18.5138 StartZ=0 EndX=50.8169 EndY=18.5138 EndZ=0
    g301: LineSegment StartX=50.8169 StartY=18.5138 StartZ=0 EndX=50.7878 EndY=18.6026 EndZ=0
    g302: LineSegment StartX=50.7878 StartY=18.6026 StartZ=0 EndX=50.7494 EndY=18.6113 EndZ=0
    g303: LineSegment StartX=50.7494 StartY=18.6113 StartZ=0 EndX=50.7397 EndY=18.6731 EndZ=0
    g304: LineSegment StartX=50.7397 StartY=18.6731 StartZ=0 EndX=50.5414 EndY=18.6536 EndZ=0
    g305: LineSegment StartX=50.5414 StartY=18.6536 StartZ=0 EndX=50.5381 EndY=18.7381 EndZ=0
    g306: LineSegment StartX=50.5381 StartY=18.7381 StartZ=0 EndX=50.4114 EndY=18.7218 EndZ=0
    g307: LineSegment StartX=50.4114 StartY=18.7218 StartZ=0 EndX=50.3951 EndY=18.7934 EndZ=0
    g308: LineSegment StartX=50.3951 StartY=18.7934 StartZ=0 EndX=50.3334 EndY=18.7934 EndZ=0
    g309: LineSegment StartX=50.3334 StartY=18.7934 StartZ=0 EndX=50.3366 EndY=18.8389 EndZ=0
    g310: LineSegment StartX=50.3366 StartY=18.8389 StartZ=0 EndX=50.2066 EndY=18.8389 EndZ=0
    g311: LineSegment StartX=50.2066 StartY=18.8389 StartZ=0 EndX=50.2099 EndY=18.9201 EndZ=0
    g312: LineSegment StartX=50.2099 StartY=18.9201 StartZ=0 EndX=50.1254 EndY=18.9266 EndZ=0
    g313: LineSegment StartX=50.1254 StartY=18.9266 StartZ=0 EndX=50.1156 EndY=19.0046 EndZ=0
    g314: LineSegment StartX=50.1156 StartY=19.0046 StartZ=0 EndX=49.9986 EndY=18.9949 EndZ=0
    g315: LineSegment StartX=49.9986 StartY=18.9949 StartZ=0 EndX=49.9921 EndY=19.0859 EndZ=0
    g316: LineSegment StartX=49.9921 StartY=19.0859 StartZ=0 EndX=49.9368 EndY=19.0501 EndZ=0
    g317: LineSegment StartX=49.9368 StartY=19.0501 StartZ=0 EndX=49.9206 EndY=19.1509 EndZ=0
    g318: LineSegment StartX=49.9206 StartY=19.1509 StartZ=0 EndX=49.7971 EndY=19.1281 EndZ=0
    g319: LineSegment StartX=49.7971 StartY=19.1281 StartZ=0 EndX=49.8068 EndY=19.2029 EndZ=0
    g320: LineSegment StartX=49.8068 StartY=19.2029 StartZ=0 EndX=49.7288 EndY=19.1899 EndZ=0
    g321: LineSegment StartX=49.7288 StartY=19.1899 StartZ=0 EndX=49.7191 EndY=19.2582 EndZ=0
    g322: LineSegment StartX=49.7191 StartY=19.2582 StartZ=0 EndX=49.6606 EndY=19.2647 EndZ=0
    g323: LineSegment StartX=49.6606 StartY=19.2647 StartZ=0 EndX=49.6541 EndY=19.3329 EndZ=0
    g324: LineSegment StartX=49.6541 StartY=19.3329 StartZ=0 EndX=49.6021 EndY=19.3329 EndZ=0
    g325: LineSegment StartX=49.6021 StartY=19.3329 StartZ=0 EndX=49.5988 EndY=19.4077 EndZ=0
    g326: LineSegment StartX=49.5988 StartY=19.4077 StartZ=0 EndX=49.4623 EndY=19.3947 EndZ=0
    g327: LineSegment StartX=49.4623 StartY=19.3947 StartZ=0 EndX=49.4623 EndY=19.4727 EndZ=0
    g328: LineSegment StartX=49.4623 StartY=19.4727 StartZ=0 EndX=49.2543 EndY=19.4532 EndZ=0
    g329: LineSegment StartX=49.2543 StartY=19.4532 StartZ=0 EndX=49.2543 EndY=19.5279 EndZ=0
    g330: LineSegment StartX=49.2543 StartY=19.5279 StartZ=0 EndX=49.199 EndY=19.5279 EndZ=0
    g331: LineSegment StartX=49.199 StartY=19.5279 StartZ=0 EndX=49.199 EndY=19.6189 EndZ=0
    g332: LineSegment StartX=49.199 StartY=19.6189 StartZ=0 EndX=49.0658 EndY=19.6059 EndZ=0
    g333: LineSegment StartX=49.0658 StartY=19.6059 StartZ=0 EndX=49.0495 EndY=19.6612 EndZ=0
    g334: LineSegment StartX=49.0495 StartY=19.6612 StartZ=0 EndX=48.991 EndY=19.6547 EndZ=0
    g335: LineSegment StartX=48.991 StartY=19.6547 StartZ=0 EndX=48.9845 EndY=19.7359 EndZ=0
    g336: LineSegment StartX=48.9845 StartY=19.7359 StartZ=0 EndX=48.8577 EndY=19.7262 EndZ=0
    g337: LineSegment StartX=48.8577 StartY=19.7262 StartZ=0 EndX=48.8577 EndY=19.8149 EndZ=0
    g338: LineSegment StartX=48.8577 StartY=19.8149 StartZ=0 EndX=48.7743 EndY=19.8069 EndZ=0
    g339: LineSegment StartX=48.7743 StartY=19.8069 StartZ=0 EndX=48.7743 EndY=19.8894 EndZ=0
    g340: LineSegment StartX=48.7743 StartY=19.8894 StartZ=0 EndX=48.5854 EndY=19.8894 EndZ=0
    g341: LineSegment StartX=48.5854 StartY=19.8894 StartZ=0 EndX=48.5854 EndY=19.9533 EndZ=0
    g342: LineSegment StartX=48.5854 StartY=19.9533 StartZ=0 EndX=48.4417 EndY=19.9533 EndZ=0
    g343: LineSegment StartX=48.4417 StartY=19.9533 StartZ=0 EndX=48.4417 EndY=20.0118 EndZ=0
    g344: LineSegment StartX=48.4417 StartY=20.0118 StartZ=0 EndX=48.3751 EndY=20.0118 EndZ=0
    g345: LineSegment StartX=48.3751 StartY=20.0118 StartZ=0 EndX=48.3751 EndY=20.089 EndZ=0
    g346: LineSegment StartX=48.3751 StartY=20.089 StartZ=0 EndX=48.3033 EndY=20.089 EndZ=0
    g347: LineSegment StartX=48.3033 StartY=20.089 StartZ=0 EndX=48.3033 EndY=20.1524 EndZ=0
    g348: LineSegment StartX=48.3033 StartY=20.1524 StartZ=0 EndX=48.0916 EndY=20.1524 EndZ=0
    g349: LineSegment StartX=48.0916 StartY=20.1524 StartZ=0 EndX=48.0916 EndY=20.2331 EndZ=0
    g350: LineSegment StartX=48.0916 StartY=20.2331 StartZ=0 EndX=47.8912 EndY=20.2331 EndZ=0
    g351: LineSegment StartX=47.8912 StartY=20.2331 StartZ=0 EndX=47.8912 EndY=20.2962 EndZ=0
    g352: LineSegment StartX=47.8912 StartY=20.2962 StartZ=0 EndX=47.6864 EndY=20.2962 EndZ=0
    g353: LineSegment StartX=47.6864 StartY=20.2962 StartZ=0 EndX=47.6864 EndY=20.3681 EndZ=0
    g354: LineSegment StartX=47.6864 StartY=20.3681 StartZ=0 EndX=47.2898 EndY=20.3681 EndZ=0
    g355: LineSegment StartX=47.2898 StartY=20.3681 StartZ=0 EndX=47.2898 EndY=20.4313 EndZ=0
    g356: LineSegment StartX=47.2898 StartY=20.4313 StartZ=0 EndX=47.0094 EndY=20.4313 EndZ=0
    g357: LineSegment StartX=47.0094 StartY=20.4313 StartZ=0 EndX=47.0094 EndY=20.5033 EndZ=0
    g358: LineSegment StartX=47.0094 StartY=20.5033 StartZ=0 EndX=46.7265 EndY=20.5033 EndZ=0
    g359: LineSegment StartX=46.7265 StartY=20.5033 StartZ=0 EndX=46.7265 EndY=20.5623 EndZ=0
    g360: LineSegment StartX=46.7265 StartY=20.5623 StartZ=0 EndX=46.3195 EndY=20.5623 EndZ=0
    g361: LineSegment StartX=46.3195 StartY=20.5623 StartZ=0 EndX=46.2304 EndY=20.478 EndZ=0
    g362: LineSegment StartX=46.2304 StartY=20.478 StartZ=0 EndX=45.8403 EndY=20.478 EndZ=0
    g363: LineSegment StartX=45.8403 StartY=20.478 StartZ=0 EndX=45.7581 EndY=20.3987 EndZ=0
    g364: LineSegment StartX=45.7581 StartY=20.3987 StartZ=0 EndX=45.6847 EndY=20.3987 EndZ=0
    g365: LineSegment StartX=45.6847 StartY=20.3987 StartZ=0 EndX=45.6847 EndY=20.4757 EndZ=0
    g366: LineSegment StartX=45.6847 StartY=20.4757 StartZ=0 EndX=45.2353 EndY=20.4757 EndZ=0
    g367: LineSegment StartX=45.2353 StartY=20.4757 StartZ=0 EndX=45.1511 EndY=20.3964 EndZ=0
    g368: LineSegment StartX=45.1511 StartY=20.3964 StartZ=0 EndX=45.039 EndY=20.3905 EndZ=0
    g369: LineSegment StartX=45.1271 StartY=20.498 StartZ=0 EndX=45.039 EndY=20.3905 EndZ=0
    g370: LineSegment StartX=45.1271 StartY=20.498 StartZ=0 EndX=45.1672 EndY=20.498 EndZ=0
    g371: LineSegment StartX=45.1672 StartY=20.498 StartZ=0 EndX=45.2586 EndY=20.5605 EndZ=0
    g372: LineSegment StartX=45.2586 StartY=20.5605 StartZ=0 EndX=45.3242 EndY=20.5605 EndZ=0
    g373: LineSegment StartX=45.3242 StartY=20.5605 StartZ=0 EndX=45.4009 EndY=20.6461 EndZ=0
    g374: LineSegment StartX=45.4009 StartY=20.6461 StartZ=0 EndX=45.5221 EndY=20.6461 EndZ=0
    g375: LineSegment StartX=45.5221 StartY=20.6461 StartZ=0 EndX=45.6149 EndY=20.705 EndZ=0
    g376: LineSegment StartX=45.6149 StartY=20.705 StartZ=0 EndX=45.8042 EndY=20.705 EndZ=0
    g377: LineSegment StartX=45.8042 StartY=20.705 StartZ=0 EndX=45.9915 EndY=20.8898 EndZ=0
    g378: LineSegment StartX=45.9915 StartY=20.8898 StartZ=0 EndX=45.9915 EndY=20.959 EndZ=0
    g379: LineSegment StartX=45.9915 StartY=20.959 StartZ=0 EndX=46.0581 EndY=21.0202 EndZ=0
    g380: LineSegment StartX=46.0581 StartY=21.0202 StartZ=0 EndX=46.0527 EndY=21.0894 EndZ=0
    g381: LineSegment StartX=46.0527 StartY=21.0894 StartZ=0 EndX=46.2124 EndY=21.2464 EndZ=0
    g382: LineSegment StartX=46.2124 StartY=21.2464 StartZ=0 EndX=46.2763 EndY=21.2277 EndZ=0
    g383: LineSegment StartX=46.2763 StartY=21.2277 StartZ=0 EndX=46.5051 EndY=21.4486 EndZ=0
    g384: LineSegment StartX=46.5051 StartY=21.4486 StartZ=0 EndX=46.585 EndY=21.4539 EndZ=0
    g385: LineSegment StartX=46.585 StartY=21.4539 StartZ=0 EndX=46.6994 EndY=21.603 EndZ=0
    g386: LineSegment StartX=46.6994 StartY=21.603 StartZ=0 EndX=46.8245 EndY=21.5843 EndZ=0
    g387: LineSegment StartX=46.8245 StartY=21.5843 StartZ=0 EndX=46.9016 EndY=21.6855 EndZ=0
    g388: LineSegment StartX=46.9016 StartY=21.6855 StartZ=0 EndX=46.9655 EndY=21.6562 EndZ=0
    g389: LineSegment StartX=46.9655 StartY=21.6562 StartZ=0 EndX=47.205 EndY=21.8754 EndZ=0
    g390: LineSegment StartX=47.205 StartY=21.8754 StartZ=0 EndX=47.205 EndY=22.0711 EndZ=0
    g391: LineSegment StartX=47.205 StartY=22.0711 StartZ=0 EndX=47.2634 EndY=22.0711 EndZ=0
    g392: LineSegment StartX=47.2634 StartY=22.0711 StartZ=0 EndX=47.6208 EndY=22.4458 EndZ=0
    g393: LineSegment StartX=47.6208 StartY=22.4458 StartZ=0 EndX=47.6208 EndY=22.5177 EndZ=0
    g394: LineSegment StartX=47.6208 StartY=22.5177 StartZ=0 EndX=47.8212 EndY=22.7182 EndZ=0
    g395: LineSegment StartX=47.8212 StartY=22.7182 StartZ=0 EndX=47.8343 EndY=22.7944 EndZ=0
    g396: LineSegment StartX=47.8343 StartY=22.7944 StartZ=0 EndX=48.0478 EndY=22.997 EndZ=0
    g397: LineSegment StartX=48.0478 StartY=22.997 StartZ=0 EndX=48.0478 EndY=23.1365 EndZ=0
    g398: LineSegment StartX=48.0478 StartY=23.1365 StartZ=0 EndX=48.0998 EndY=23.2173 EndZ=0
    g399: LineSegment StartX=48.0998 StartY=23.2173 StartZ=0 EndX=48.0998 EndY=23.2802 EndZ=0
    ... +484 more geometry lines
  constraints (1492):
    c: Coincident(g3,g2)
    c: Vertical(g4)
    c: Vertical(g6)
    c: Coincident(g8,g7)
    c: Vertical(g8)
    c: Coincident(g8,g9)
    c: Coincident(g9,g10)
    c: Vertical(g10)
    c: Coincident(g10,g11)
    c: Coincident(g11,g12)
    c: Vertical(g12)
    c: Coincident(g13,g12)
    c: Horizontal(g13)
    c: Vertical(g14)
    c: Coincident(g16,g15)
    c: Vertical(g16)
    c: Horizontal(g17)
    c: Coincident(g18,g17)
    c: Vertical(g18)
    c: Horizontal(g19)
    c: Coincident(g20,g19)
    c: Vertical(g20)
    c: Horizontal(g21)
    c: Vertical(g22)
    c: Horizontal(g23)
    c: Coincident(g24,g23)
    c: Vertical(g24)
    c: Horizontal(g25)
    c: Coincident(g27,g26)
    c: Horizontal(g27)
    c: Vertical(g28)
    c: Coincident(g30,g29)
    c: Vertical(g30)
    c: Coincident(g31,g32)
    c: Vertical(g32)
    c: Coincident(g32,g33)
    c: Horizontal(g33)
    c: Coincident(g34,g33)
    c: Vertical(g34)
    c: Coincident(g35,g34)
    c: Horizontal(g35)
    c: Coincident(g36,g35)
    c: Vertical(g36)
    c: Coincident(g37,g36)
    c: Horizontal(g37)
    c: Vertical(g38)
    c: Horizontal(g39)
    c: Vertical(g40)
    c: Horizontal(g41)
    c: Coincident(g42,g41)
    c: Vertical(g42)
    c: Horizontal(g43)
    c: Coincident(g44,g43)
    c: Vertical(g44)
    c: Coincident(g45,g44)
    c: Horizontal(g45)
    c: Coincident(g46,g45)
    c: Vertical(g46)
    c: Coincident(g47,g46)
    c: Horizontal(g47)
    c: Coincident(g48,g47)
    c: Vertical(g48)
    c: Horizontal(g49)
    c: Vertical(g50)
    c: Coincident(g51,g50)
    c: Horizontal(g51)
    c: Vertical(g52)
    c: Coincident(g53,g52)
    c: Horizontal(g53)
    c: Coincident(g54,g53)
    c: Vertical(g54)
    c: Coincident(g55,g54)
    c: Horizontal(g55)
    c: Coincident(g56,g55)
    c: Vertical(g56)
    c: Coincident(g57,g56)
    c: Horizontal(g57)
    c: Coincident(g58,g57)
    c: Vertical(g58)
    c: Coincident(g60,g59)
    c: Vertical(g60)
    c: Coincident(g61,g60)
    c: Horizontal(g61)
    c: Vertical(g62)
    c: Horizontal(g63)
    c: Coincident(g64,g63)
    c: Vertical(g64)
    c: Horizontal(g65)
    c: Vertical(g66)
    c: Coincident(g68,g67)
    c: Vertical(g68)
    c: Horizontal(g69)
    c: Coincident(g70,g69)
    c: Vertical(g70)
    c: Horizontal(g71)
    c: Coincident(g72,g71)
    c: Vertical(g72)
    c: Horizontal(g73)
    c: Coincident(g74,g73)
    c: Vertical(g74)
    c: Horizontal(g75)
    c: Coincident(g76,g75)
    c: Vertical(g76)
    c: Horizontal(g77)
    c: Vertical(g78)
    c: Coincident(g79,g78)
    c: Coincident(g80,g79)
    c: Vertical(g80)
    c: Coincident(g81,g80)
    c: Coincident(g82,g81)
    c: Horizontal(g83)
    c: Coincident(g85,g84)
    c: Horizontal(g85)
    c: Coincident(g86,g85)
    c: Coincident(g89,g88)
    c: Horizontal(g89)
    c: Coincident(g90,g89)
    c: Coincident(g91,g90)
    c: Horizontal(g91)
    c: Coincident(g92,g91)
    c: Horizontal(g93)
    c: Coincident(g94,g93)
    c: Horizontal(g95)
    c: Coincident(g96,g95)
    c: Coincident(g97,g98)
    c: Coincident(g98,g99)
    c: Vertical(g99)
    c: Coincident(g99,g100)
    c: Coincident(g100,g101)
    c: Coincident(g101,g102)
    c: Coincident(g102,g103)
    c: Coincident(g103,g104)
    c: Coincident(g104,g105)
    c: Vertical(g105)
    c: Coincident(g105,g106)
    c: Coincident(g106,g107)
    c: Coincident(g107,g108)
    c: Horizontal(g108)
    c: Coincident(g108,g109)
    c: Coincident(g109,g110)
    c: Vertical(g110)
    c: Coincident(g110,g111)
    c: Coincident(g111,g112)
    c: Coincident(g112,g113)
    c: Coincident(g113,g114)
    c: Coincident(g114,g115)
    c: Coincident(g115,g116)
    c: Vertical(g116)
    c: Coincident(g116,g117)
    c: Coincident(g117,g118)
    c: Coincident(g118,g119)
    c: Coincident(g119,g120)
    c: Coincident(g120,g121)
    c: Horizontal(g121)
    c: Coincident(g121,g122)
    c: Coincident(g122,g123)
    c: Coincident(g123,g124)
    c: Coincident(g124,g125)
    c: Vertical(g125)
    c: Coincident(g125,g126)
    c: Coincident(g126,g127)
    c: Horizontal(g127)
    c: Coincident(g127,g128)
    c: Vertical(g128)
    c: Coincident(g128,g129)
    c: Coincident(g129,g130)
    c: Vertical(g130)
    c: Coincident(g130,g131)
    c: Horizontal(g131)
    c: Coincident(g131,g132)
    c: Vertical(g132)
    c: Coincident(g132,g133)
    c: Coincident(g133,g134)
    c: Coincident(g134,g135)
    c: Coincident(g135,g136)
    c: Coincident(g136,g137)
    c: Coincident(g137,g138)
    c: Vertical(g138)
    c: Coincident(g138,g139)
    c: Coincident(g139,g140)
    c: Vertical(g140)
    c: Coincident(g140,g141)
    c: Horizontal(g141)
    c: Coincident(g141,g142)
    c: Coincident(g142,g143)
    c: Coincident(g143,g144)
    c: Coincident(g144,g145)
    c: Coincident(g145,g146)
    c: Vertical(g146)
    c: Coincident(g146,g147)
    c: Coincident(g147,g148)
    c: Vertical(g148)
    c: Coincident(g148,g149)
    c: Horizontal(g149)
    c: Coincident(g149,g150)
    c: Vertical(g150)
    c: Coincident(g150,g151)
    c: Horizontal(g151)
    c: Coincident(g151,g152)
    c: Vertical(g152)
    c: Coincident(g152,g153)
    c: Horizontal(g153)
    c: Coincident(g153,g154)
    c: Vertical(g154)
    c: Coincident(g154,g155)
    c: Horizontal(g155)
    c: Coincident(g155,g156)
    c: Vertical(g156)
    c: Coincident(g156,g157)
    c: Horizontal(g157)
    c: Coincident(g157,g158)
    c: Vertical(g158)
    c: Coincident(g158,g159)
    c: Coincident(g159,g160)
    c: Coincident(g160,g161)
    c: Horizontal(g161)
    c: Coincident(g161,g162)
    c: Vertical(g162)
    c: Coincident(g162,g163)
    c: Horizontal(g163)
    c: Coincident(g163,g164)
    c: Coincident(g164,g165)
    c: Horizontal(g165)
    c: Coincident(g165,g166)
    c: Vertical(g166)
    c: Coincident(g166,g167)
    c: Horizontal(g167)
    c: Coincident(g167,g168)
    c: Coincident(g168,g169)
    c: Coincident(g169,g170)
    c: Vertical(g170)
    c: Coincident(g170,g171)
    c: Coincident(g171,g172)
    c: Vertical(g172)
    c: Coincident(g172,g173)
    c: Horizontal(g173)
    c: Coincident(g173,g174)
    c: Vertical(g174)
    c: Coincident(g174,g175)
    c: Horizontal(g175)
    c: Coincident(g175,g176)
    c: Vertical(g176)
    c: Coincident(g176,g177)
    c: Coincident(g177,g178)
    c: Vertical(g178)
    c: Coincident(g178,g179)
    c: Horizontal(g179)
    c: Coincident(g179,g180)
    c: Vertical(g180)
    c: Coincident(g180,g181)
    c: Horizontal(g181)
    c: Coincident(g181,g182)
    c: Vertical(g182)
    c: Coincident(g182,g183)
    c: Horizontal(g183)
    c: Coincident(g183,g184)
    c: Vertical(g184)
    c: Coincident(g184,g185)
    c: Horizontal(g185)
    c: Coincident(g185,g186)
    c: Coincident(g186,g187)
    c: Coincident(g187,g188)
    c: Coincident(g188,g189)
    c: Vertical(g189)
    c: Coincident(g189,g190)
    c: Coincident(g190,g191)
    c: Coincident(g191,g192)
    c: Coincident(g192,g193)
    c: Coincident(g193,g194)
    c: Coincident(g194,g195)
    c: Vertical(g195)
    c: Coincident(g195,g196)
    c: Coincident(g196,g197)
    c: Vertical(g197)
    c: Coincident(g197,g198)
    c: Coincident(g198,g199)
    c: Vertical(g199)
    c: Coincident(g199,g200)
    c: Coincident(g200,g201)
    c: Vertical(g201)
    c: Coincident(g201,g202)
    c: Coincident(g202,g203)
    c: Vertical(g203)
    c: Coincident(g203,g204)
    c: Coincident(g204,g205)
    c: Vertical(g205)
    c: Coincident(g205,g206)
    c: Coincident(g206,g207)
    c: Coincident(g207,g208)
    c: Coincident(g208,g209)
    c: Vertical(g209)
    c: Coincident(g209,g210)
    c: Coincident(g210,g211)
    c: Coincident(g211,g212)
    c: Coincident(g212,g213)
    c: Coincident(g213,g214)
    c: Coincident(g214,g215)
    c: Vertical(g215)
    c: Coincident(g215,g216)
    c: Coincident(g216,g217)
    c: Horizontal(g217)
    c: Coincident(g217,g218)
    c: Vertical(g218)
    c: Coincident(g218,g219)
    c: Horizontal(g219)
    c: Coincident(g219,g220)
    c: Coincident(g220,g221)
    c: Horizontal(g221)
    c: Coincident(g221,g222)
    c: Coincident(g222,g223)
    c: Horizontal(g223)
    c: Coincident(g223,g224)
    c: Coincident(g224,g225)
    c: Horizontal(g225)
    c: Coincident(g225,g226)
    c: Vertical(g226)
    c: Coincident(g226,g227)
    c: Horizontal(g227)
    c: Coincident(g227,g228)
    c: Vertical(g228)
    c: Coincident(g228,g229)
    c: Horizontal(g229)
    c: Coincident(g229,g230)
    c: Coincident(g230,g231)
    c: Coincident(g231,g232)
    c: Coincident(g232,g233)
    c: Horizontal(g233)
    c: Coincident(g233,g234)
    c: Coincident(g234,g235)
    c: Horizontal(g235)
    c: Coincident(g235,g236)
    c: Coincident(g236,g237)
    c: Horizontal(g237)
    c: Coincident(g237,g238)
    c: Coincident(g238,g239)
    c: Horizontal(g239)
    c: Coincident(g239,g240)
    c: Coincident(g240,g241)
    c: Vertical(g241)
    c: Coincident(g241,g242)
    c: Horizontal(g242)
    c: Coincident(g242,g243)
    c: Vertical(g243)
    c: Coincident(g243,g244)
    c: Coincident(g244,g245)
    c: Vertical(g245)
    c: Coincident(g245,g246)
    c: Horizontal(g246)
    c: Coincident(g246,g247)
    c: Coincident(g247,g248)
    c: Horizontal(g248)
    c: Coincident(g248,g249)
    c: Vertical(g249)
    c: Coincident(g249,g250)
    c: Coincident(g250,g251)
    c: Coincident(g251,g252)
    c: Horizontal(g252)
    c: Coincident(g252,g253)
    c: Coincident(g253,g254)
    c: Horizontal(g254)
    c: Coincident(g254,g255)
    c: Vertical(g255)
    c: Coincident(g255,g256)
    c: Coincident(g256,g257)
    c: Coincident(g257,g258)
    c: Coincident(g258,g259)
    c: Coincident(g259,g260)
    c: Coincident(g260,g261)
    c: Vertical(g257)
    c: Horizontal(g258)
    c: Horizontal(g256)
    c: Vertical(g259)
    c: Horizontal(g260)
    c: Vertical(g261)
    c: Coincident(g261,g262)
    c: Horizontal(g262)
    c: Coincident(g262,g263)
    c: Vertical(g263)
    c: Coincident(g263,g264)
    c: Coincident(g264,g265)
    c: Coincident(g265,g266)
    c: Coincident(g266,g267)
    c: Coincident(g267,g268)
    c: Coincident(g268,g269)
    c: Vertical(g269)
    c: Coincident(g269,g270)
    c: Horizontal(g270)
    c: Coincident(g270,g271)
    c: Vertical(g271)
    c: Coincident(g271,g272)
    c: Coincident(g272,g273)
    c: Vertical(g273)
    c: Coincident(g273,g274)
    c: Horizontal(g274)
    c: Coincident(g274,g275)
    c: Vertical(g275)
    c: Coincident(g275,g276)
    c: Horizontal(g276)
    c: Coincident(g276,g277)
    c: Coincident(g277,g278)
    c: Horizontal(g278)
    c: Coincident(g278,g279)
    c: Coincident(g279,g280)
    c: Coincident(g280,g281)
    c: Vertical(g281)
    c: Coincident(g281,g282)
    c: Coincident(g282,g283)
    c: Coincident(g283,g284)
    c: Horizontal(g284)
    c: Coincident(g284,g285)
    c: Coincident(g285,g286)
    c: Coincident(g286,g287)
    c: Coincident(g287,g288)
    c: Coincident(g288,g289)
    c: Coincident(g289,g290)
    c: Coincident(g290,g291)
    c: Vertical(g291)
    c: Coincident(g291,g292)
    c: Horizontal(g292)
    c: Coincident(g292,g293)
    c: Coincident(g293,g294)
    c: Horizontal(g294)
    c: Coincident(g294,g295)
    c: Vertical(g295)
    c: Coincident(g295,g296)
    c: Coincident(g296,g297)
    c: Vertical(g297)
    c: Coincident(g297,g298)
    c: Horizontal(g298)
    c: Coincident(g298,g299)
    c: Vertical(g299)
    c: Coincident(g299,g300)
    c: Horizontal(g300)
    c: Coincident(g300,g301)
    c: Coincident(g301,g302)
    c: Coincident(g302,g303)
    c: Coincident(g303,g304)
    c: Coincident(g304,g305)
    c: Coincident(g305,g306)
    c: Coincident(g306,g307)
    c: Coincident(g307,g308)
    c: Horizontal(g308)
    c: Coincident(g308,g309)
    c: Coincident(g309,g310)
    c: Horizontal(g310)
    c: Coincident(g310,g311)
    c: Coincident(g311,g312)
    c: Coincident(g312,g313)
    c: Coincident(g313,g314)
    c: Coincident(g314,g315)
    c: Coincident(g315,g316)
    c: Coincident(g316,g317)
    c: Coincident(g317,g318)
    c: Coincident(g318,g319)
    c: Coincident(g319,g320)
    c: Coincident(g320,g321)
    c: Coincident(g321,g322)
    c: Coincident(g322,g323)
    c: Coincident(g323,g324)
    c: Horizontal(g324)
    c: Coincident(g324,g325)
    c: Coincident(g325,g326)
    c: Coincident(g326,g327)
    c: Vertical(g327)
    c: Coincident(g327,g328)
    c: Coincident(g328,g329)
    c: Coincident(g329,g330)
    c: Coincident(g330,g331)
    c: Vertical(g331)
    c: Coincident(g331,g332)
    c: Coincident(g332,g333)
    c: Coincident(g333,g334)
    c: Coincident(g334,g335)
    c: Coincident(g335,g336)
    c: Coincident(g336,g337)
    c: Vertical(g337)
    c: Coincident(g337,g338)
    c: Coincident(g338,g339)
    c: Coincident(g339,g340)
    c: Coincident(g340,g341)
    c: Coincident(g341,g342)
    c: Coincident(g342,g343)
    c: Coincident(g343,g344)
    c: Coincident(g344,g345)
    c: Coincident(g345,g346)
    c: Coincident(g346,g347)
    c: Coincident(g347,g348)
    c: Coincident(g348,g349)
    c: Coincident(g349,g350)
    c: Coincident(g350,g351)
    c: Coincident(g351,g352)
    c: Coincident(g352,g353)
    c: Coincident(g353,g354)
    c: Coincident(g354,g355)
    c: Coincident(g355,g356)
    c: Coincident(g356,g357)
    c: Vertical(g357)
    c: Coincident(g357,g358)
    c: Horizontal(g358)
    c: Coincident(g358,g359)
    c: Coincident(g359,g360)
    c: Coincident(g360,g361)
    c: Coincident(g361,g362)
    c: Horizontal(g362)
    c: Coincident(g362,g363)
    c: Coincident(g363,g364)
    c: Coincident(g364,g365)
    c: Coincident(g365,g366)
    c: Coincident(g366,g367)
    c: Horizontal(g290)
    c: Vertical(g287)
    c: Vertical(g285)
    c: Vertical(g283)
    c: Vertical(g279)
    c: Vertical(g277)
    c: Horizontal(g286)
    c: Horizontal(g288)
    c: Vertical(g289)
    c: Horizontal(g280)
    c: Horizontal(g282)
    c: Vertical(g329)
    c: Horizontal(g330)
    c: Horizontal(g340)
    c: Horizontal(g342)
    c: Horizontal(g344)
    c: Horizontal(g346)
    c: Horizontal(g348)
    c: Horizontal(g350)
    c: Vertical(g339)
    c: Vertical(g341)
    c: Vertical(g343)
    c: Vertical(g345)
    c: Vertical(g347)
    c: Vertical(g349)
    c: Vertical(g351)
    c: Vertical(g353)
    c: Vertical(g355)
    c: Horizontal(g352)
    c: Horizontal(g354)
    c: Horizontal(g356)
    c: Vertical(g359)
    c: Horizontal(g360)
    c: Horizontal(g364)
    c: Vertical(g365)
    c: Horizontal(g366)
    c: Coincident(g368,g367)
    c: Coincident(g369,g368)
    c: Coincident(g369,g370)
    c: Coincident(g370,g371)
    c: Coincident(g371,g372)
    c: Horizontal(g372)
    c: Coincident(g372,g373)
    c: Coincident(g373,g374)
    c: Coincident(g374,g375)
    c: Coincident(g375,g376)
    c: Coincident(g376,g377)
    c: Coincident(g377,g378)
    c: Vertical(g378)
    c: Coincident(g378,g379)
    c: Coincident(g379,g380)
    c: Coincident(g380,g381)
    c: Coincident(g381,g382)
    c: Coincident(g382,g383)
    c: Coincident(g383,g384)
    c: Coincident(g384,g385)
    c: Coincident(g385,g386)
    c: Coincident(g386,g387)
    c: Coincident(g387,g388)
    c: Coincident(g388,g389)
    c: Coincident(g389,g390)
    c: Coincident(g390,g391)
    c: Horizontal(g391)
    c: Coincident(g391,g392)
    c: Coincident(g392,g393)
    c: Coincident(g393,g394)
    c: Coincident(g394,g395)
    c: Coincident(g395,g396)
    c: Coincident(g396,g397)
    c: Coincident(g397,g398)
    c: Coincident(g398,g399)
    c: Coincident(g399,g400)
    c: Coincident(g400,g401)
    c: Coincident(g401,g402)
    c: Coincident(g402,g403)
    c: Coincident(g403,g404)
    c: Coincident(g404,g405)
    c: Coincident(g405,g406)
    c: Coincident(g406,g407)
    c: Coincident(g407,g408)
    c: Coincident(g408,g409)
    c: Vertical(g409)
    c: Coincident(g409,g410)
    c: Coincident(g410,g411)
    c: Vertical(g411)
    c: Coincident(g411,g412)
    c: Horizontal(g412)
    c: Coincident(g412,g413)
    c: Coincident(g413,g414)
    c: Horizontal(g414)
    c: Coincident(g414,g415)
    c: Coincident(g415,g416)
    c: Coincident(g416,g417)
    c: Coincident(g417,g418)
    c: Coincident(g418,g419)
    c: Coincident(g419,g420)
    c: Coincident(g420,g421)
    c: Coincident(g421,g422)
    c: Coincident(g422,g423)
    c: Coincident(g423,g424)
    c: Coincident(g424,g425)
    c: Coincident(g425,g426)
    c: Horizontal(g426)
    c: Coincident(g426,g427)
    c: Coincident(g427,g428)
    c: Horizontal(g428)
    c: Coincident(g428,g429)
    c: Coincident(g429,g430)
    c: Coincident(g430,g431)
    c: Coincident(g431,g432)
    c: Horizontal(g432)
    c: Coincident(g432,g433)
    c: Coincident(g433,g434)
    c: Horizontal(g434)
    c: Coincident(g434,g435)
    c: Coincident(g435,g436)
    c: Coincident(g436,g437)
    c: Coincident(g437,g438)
    c: Coincident(g439,g440)
    c: Coincident(g440,g441)
    c: Coincident(g441,g442)
    c: Coincident(g442,g443)
    c: Coincident(g443,g444)
    c: Coincident(g444,g445)
    c: Coincident(g445,g446)
    c: Coincident(g446,g447)
    c: Coincident(g447,g448)
    c: Coincident(g448,g449)
    c: Coincident(g449,g450)
    c: Coincident(g450,g451)
    c: Coincident(g451,g452)
    c: Coincident(g452,g453)
    c: Coincident(g453,g454)
    c: Coincident(g454,g455)
    c: Coincident(g455,g456)
    c: Coincident(g456,g457)
    c: Coincident(g457,g458)
    c: Coincident(g458,g459)
    c: Coincident(g459,g460)
    c: Coincident(g460,g461)
    c: Coincident(g461,g462)
    c: Coincident(g462,g463)
    c: Coincident(g463,g464)
    c: Coincident(g464,g465)
    c: Coincident(g465,g466)
    c: Coincident(g466,g467)
    c: Coincident(g467,g468)
    c: Coincident(g468,g469)
    c: Coincident(g469,g470)
    c: Coincident(g470,g471)
    c: Coincident(g471,g472)
    c: Horizontal(g472)
    c: Coincident(g472,g473)
    c: Coincident(g473,g474)
    c: Coincident(g474,g475)
    c: Coincident(g475,g476)
    c: Coincident(g476,g477)
    c: Coincident(g477,g478)
    c: Coincident(g478,g479)
    c: Coincident(g479,g480)
    c: Coincident(g480,g481)
    c: Coincident(g481,g482)
    c: Coincident(g482,g483)
    c: Coincident(g483,g484)
    c: Coincident(g484,g485)
    c: Coincident(g485,g486)
    c: Coincident(g486,g487)
    c: Coincident(g487,g488)
    c: Vertical(g488)
    c: Coincident(g488,g489)
    c: Coincident(g489,g490)
    c: Vertical(g490)
    c: Coincident(g490,g491)
    c: Coincident(g491,g492)
    c: Coincident(g492,g493)
    c: Coincident(g493,g494)
    c: Coincident(g494,g495)
    c: Coincident(g495,g496)
    c: Coincident(g496,g497)
    c: Coincident(g497,g498)
    c: Coincident(g498,g499)
    c: Coincident(g499,g500)
    c: Coincident(g500,g501)
    c: Coincident(g501,g502)
    c: Coincident(g502,g503)
    c: Coincident(g503,g504)
    c: Horizontal(g370)
    c: Horizontal(g374)
    c: Horizontal(g376)
    c: Vertical(g390)
    c: Vertical(g397)
    c: Vertical(g399)
    c: Vertical(g401)
    c: Vertical(g403)
    c: Vertical(g407)
    c: Horizontal(g410)
    c: Vertical(g413)
    c: Vertical(g415)
    c: Horizontal(g416)
    c: Vertical(g417)
    c: Horizontal(g418)
    c: Vertical(g419)
    c: Vertical(g421)
    c: Vertical(g423)
    c: Vertical(g425)
    c: Vertical(g427)
    c: Vertical(g429)
    c: Horizontal(g420)
    c: Horizontal(g422)
    c: Horizontal(g424)
    c: Vertical(g431)
    c: Vertical(g433)
    c: Vertical(g435)
    c: Horizontal(g436)
    c: Horizontal(g438)
    c: Vertical(g437)
    c: Coincident(g439,g505)
    c: Horizontal(g505)
    c: Coincident(g505,g506)
    c: Coincident(g506,g438)
    c: Vertical(g506)
    c: Horizontal(g464)
    c: Horizontal(g462)
    c: Horizontal(g460)
    c: Horizontal(g458)
    c: Horizontal(g456)
    c: Horizontal(g454)
    c: Horizontal(g452)
    c: Horizontal(g450)
    c: Horizontal(g448)
    c: Horizontal(g446)
    c: Horizontal(g444)
    c: Horizontal(g442)
    c: Horizontal(g440)
    c: Horizontal(g468)
    c: Horizontal(g470)
    c: Horizontal(g474)
    c: Horizontal(g476)
    c: Horizontal(g478)
    c: Vertical(g465)
    c: Horizontal(g466)
    c: Vertical(g475)
    c: Vertical(g477)
    c: Horizontal(g491)
    c: Horizontal(g496)
    c: Horizontal(g494)
    c: Horizontal(g498)
    c: Vertical(g499)
    c: Vertical(g497)
    c: Vertical(g495)
    c: Vertical(g493)
    c: Horizontal(g500)
    c: Horizontal(g502)
    c: Horizontal(g504)
    c: Vertical(g501)
    c: Vertical(g503)
    c: Coincident(g504,g507)
    c: Vertical(g507)
    c: Coincident(g507,g508)
    c: Coincident(g508,g509)
    c: Coincident(g509,g510)
    c: Coincident(g510,g511)
    c: Vertical(g511)
    c: Coincident(g511,g512)
    c: Horizontal(g512)
    c: Coincident(g512,g513)
    c: Vertical(g513)
    c: Coincident(g513,g514)
    c: Coincident(g514,g515)
    c: Vertical(g515)
    c: Coincident(g515,g516)
    c: Horizontal(g516)
    c: Coincident(g516,g517)
    c: Coincident(g517,g518)
    c: Horizontal(g518)
    c: Coincident(g518,g519)
    c: Coincident(g519,g520)
    c: Coincident(g521,g522)
    c: Coincident(g522,g523)
    c: Coincident(g523,g524)
    c: Coincident(g524,g525)
    c: Coincident(g525,g526)
    c: Coincident(g526,g527)
    c: Coincident(g527,g528)
    c: Coincident(g528,g529)
    c: Coincident(g529,g530)
    c: Coincident(g531,g532)
    c: Coincident(g532,g533)
    c: Coincident(g533,g534)
    c: Coincident(g534,g535)
    c: Coincident(g535,g536)
    c: Coincident(g536,g537)
    c: Coincident(g537,g538)
    c: Coincident(g538,g539)
    c: Coincident(g539,g540)
    c: Coincident(g540,g541)
    c: Coincident(g541,g542)
    c: Coincident(g542,g543)
    c: Coincident(g543,g544)
    c: Coincident(g544,g545)
    c: Coincident(g545,g546)
    c: Coincident(g546,g547)
    c: Coincident(g547,g548)
    c: Coincident(g548,g549)
    c: Coincident(g549,g550)
    c: Horizontal(g550)
    c: Coincident(g550,g551)
    c: Coincident(g551,g552)
    c: Coincident(g552,g553)
    c: Coincident(g553,g554)
    c: Horizontal(g554)
    c: Coincident(g554,g555)
    c: Coincident(g555,g556)
    c: Coincident(g556,g557)
    c: Coincident(g557,g558)
    c: Horizontal(g558)
    c: Coincident(g558,g559)
    c: Coincident(g559,g560)
    c: Coincident(g560,g561)
    c: Coincident(g562,g563)
    c: Horizontal(g563)
    c: Coincident(g563,g564)
    c: Coincident(g564,g565)
    c: Coincident(g565,g566)
    c: Coincident(g566,g567)
    c: Horizontal(g567)
    c: Coincident(g567,g568)
    c: Coincident(g568,g569)
    c: Coincident(g569,g570)
    c: Coincident(g570,g571)
    c: Coincident(g571,g572)
    c: Coincident(g572,g573)
    c: Coincident(g573,g574)
    c: Coincident(g574,g575)
    c: Coincident(g575,g576)
    c: Coincident(g576,g577)
    c: Coincident(g577,g578)
    c: Coincident(g578,g579)
    c: Coincident(g579,g580)
    c: Vertical(g580)
    c: Coincident(g580,g581)
    c: Coincident(g581,g582)
    c: Coincident(g582,g583)
    c: Coincident(g583,g584)
    c: Coincident(g584,g585)
    c: Horizontal(g585)
    c: Coincident(g585,g586)
    c: Coincident(g586,g587)
    c: Coincident(g587,g588)
    c: Vertical(g588)
    c: Coincident(g588,g589)
    c: Coincident(g589,g590)
    c: Coincident(g590,g591)
    c: Coincident(g592,g593)
    c: Horizontal(g593)
    c: Coincident(g593,g594)
    c: Coincident(g594,g595)
    c: Coincident(g595,g596)
    c: Vertical(g596)
    c: Coincident(g596,g597)
    c: Horizontal(g597)
    c: Coincident(g597,g598)
    c: Vertical(g598)
    c: Coincident(g598,g599)
    c: Coincident(g599,g600)
    c: Coincident(g600,g601)
    c: Horizontal(g601)
    c: Coincident(g601,g602)
    c: Coincident(g602,g603)
    c: Coincident(g603,g604)
    c: Coincident(g604,g605)
    c: Coincident(g605,g606)
    c: Coincident(g606,g607)
    c: Coincident(g607,g608)
    c: Coincident(g608,g609)
    c: Horizontal(g609)
    c: Coincident(g609,g610)
    c: Coincident(g610,g611)
    c: Coincident(g611,g612)
    c: Coincident(g612,g613)
    c: Vertical(g613)
    c: Coincident(g613,g614)
    c: Coincident(g614,g615)
    c: Vertical(g615)
    c: Coincident(g615,g616)
    c: Coincident(g616,g617)
    c: Vertical(g617)
    c: Coincident(g618,g619)
    c: Vertical(g619)
    c: Coincident(g619,g620)
    c: Coincident(g620,g621)
    c: Coincident(g621,g622)
    c: Coincident(g622,g623)
    c: Coincident(g623,g624)
    c: Coincident(g624,g625)
    c: Coincident(g625,g626)
    c: Coincident(g626,g627)
    c: Vertical(g627)
    c: Coincident(g627,g628)
    c: Coincident(g628,g629)
    c: Coincident(g629,g630)
    c: Coincident(g630,g631)
    c: Coincident(g631,g632)
    c: Coincident(g632,g633)
    c: Vertical(g633)
    c: Coincident(g633,g634)
    c: Coincident(g634,g635)
    c: Vertical(g635)
    c: Coincident(g635,g636)
    c: Coincident(g636,g637)
    c: Coincident(g637,g638)
    c: Coincident(g638,g639)
    c: Coincident(g639,g640)
    c: Horizontal(g640)
    c: Coincident(g640,g641)
    c: Coincident(g641,g642)
    c: Vertical(g642)
    c: Coincident(g642,g643)
    c: Coincident(g643,g644)
    c: Vertical(g644)
    c: Coincident(g644,g645)
    c: Coincident(g645,g646)
    c: Coincident(g646,g647)
    c: Coincident(g647,g648)
    c: Coincident(g648,g649)
    c: Coincident(g649,g650)
    c: Coincident(g650,g651)
    c: Coincident(g651,g652)
    c: Vertical(g652)
    c: Coincident(g652,g653)
    c: Coincident(g653,g654)
    c: Coincident(g654,g655)
    c: Coincident(g655,g656)
    c: Coincident(g656,g657)
    c: Coincident(g657,g658)
    c: Vertical(g658)
    c: Coincident(g658,g659)
    c: Coincident(g659,g660)
    c: Vertical(g660)
    c: Coincident(g660,g661)
    c: Coincident(g661,g662)
    c: Coincident(g662,g663)
    c: Coincident(g663,g664)
    c: Coincident(g664,g665)
    c: Coincident(g665,g666)
    c: Coincident(g666,g667)
    c: Coincident(g667,g668)
    c: Coincident(g668,g669)
    c: Coincident(g669,g670)
    c: Coincident(g670,g671)
    c: Coincident(g671,g672)
    c: Coincident(g672,g673)
    c: Horizontal(g673)
    c: Coincident(g673,g674)
    c: Coincident(g674,g675)
    c: Coincident(g675,g676)
    c: Coincident(g676,g677)
    c: Coincident(g677,g678)
    c: Vertical(g678)
    c: Coincident(g678,g679)
    c: Coincident(g680,g681)
    c: Vertical(g681)
    c: Coincident(g681,g682)
    c: Horizontal(g682)
    c: Coincident(g682,g683)
    c: Coincident(g683,g684)
    c: Coincident(g684,g685)
    c: Coincident(g685,g686)
    c: Coincident(g686,g687)
    c: Vertical(g687)
    c: Coincident(g687,g688)
    c: Coincident(g688,g689)
    c: Coincident(g689,g690)
    c: Coincident(g690,g691)
    c: Coincident(g691,g692)
    c: Coincident(g692,g693)
    c: Coincident(g693,g694)
    c: Horizontal(g694)
    c: Coincident(g694,g695)
    c: Horizontal(g508)
    c: Vertical(g509)
    c: Horizontal(g510)
    c: Vertical(g519)
    c: Vertical(g517)
    c: Horizontal(g520)
    c: Coincident(g520,g696)
    c: Coincident(g696,g697)
    c: Horizontal(g697)
    c: Coincident(g697,g698)
    c: Coincident(g698,g521)
    c: Vertical(g698)
    c: Vertical(g522)
    c: Vertical(g524)
    c: Vertical(g526)
    c: Horizontal(g523)
    c: Horizontal(g525)
    c: Horizontal(g527)
    c: Horizontal(g529)
    c: Horizontal(g532)
    c: Horizontal(g521)
    c: Vertical(g528)
    c: Vertical(g530)
    c: Coincident(g530,g699)
    c: Coincident(g699,g700)
    c: Coincident(g700,g701)
    c: Coincident(g701,g531)
    c: Vertical(g700)
    c: Vertical(g531)
    c: Vertical(g533)
    c: Vertical(g535)
    c: Vertical(g537)
    c: Vertical(g539)
    c: Vertical(g541)
    c: Horizontal(g534)
    c: Horizontal(g536)
    c: Horizontal(g538)
    c: Horizontal(g540)
    c: Horizontal(g542)
    c: Horizontal(g544)
    c: Horizontal(g546)
    c: Horizontal(g699)
    c: Horizontal(g701)
    c: Vertical(g543)
    c: Vertical(g545)
    c: Vertical(g547)
    c: Vertical(g549)
    c: Horizontal(g548)
    c: Vertical(g555)
    c: Vertical(g553)
    c: Vertical(g551)
    c: Horizontal(g552)
    c: Horizontal(g556)
    c: Horizontal(g560)
    c: Vertical(g557)
    c: Vertical(g559)
    c: Vertical(g561)
    c: Coincident(g702,g562)
    c: Coincident(g702,g561)
    c: Horizontal(g565)
    c: Horizontal(g569)
    c: Horizontal(g571)
    c: Horizontal(g573)
    c: Horizontal(g575)
    c: Horizontal(g702)
    c: Vertical(g566)
    c: Vertical(g568)
    c: Vertical(g570)
    c: Vertical(g572)
    c: Vertical(g574)
    c: Vertical(g576)
    c: Vertical(g578)
    c: Vertical(g582)
    c: Vertical(g584)
    c: Horizontal(g577)
    c: Horizontal(g579)
    c: Horizontal(g581)
    c: Horizontal(g583)
    c: Horizontal(g587)
    c: Horizontal(g589)
    c: Horizontal(g591)
    c: Coincident(g591,g592)
    c: Vertical(g590)
    c: Vertical(g592)
    c: Vertical(g594)
    c: Vertical(g602)
    c: Vertical(g604)
    c: Horizontal(g595)
    c: Horizontal(g599)
    c: Horizontal(g605)
    c: Horizontal(g607)
    c: Vertical(g608)
    c: Vertical(g611)
    c: Horizontal(g612)
    c: Horizontal(g614)
    c: Horizontal(g620)
    c: Horizontal(g622)
    c: Vertical(g621)
    c: Vertical(g623)
    c: Coincident(g618,g703)
    c: Vertical(g703)
    c: Coincident(g703,g704)
    c: Horizontal(g704)
    c: Coincident(g704,g617)
    c: Horizontal(g624)
    c: Vertical(g625)
    c: Horizontal(g643)
    c: Horizontal(g645)
    c: Horizontal(g647)
    c: Horizontal(g649)
    c: Horizontal(g651)
    c: Horizontal(g653)
    c: Horizontal(g655)
    c: Horizontal(g657)
    c: Horizontal(g659)
    c: Vertical(g656)
    c: Vertical(g654)
    c: Vertical(g650)
    c: Vertical(g648)
    c: Vertical(g646)
    c: Vertical(g637)
    c: Vertical(g639)
    c: Horizontal(g661)
    c: Horizontal(g663)
    c: Horizontal(g665)
    c: Horizontal(g667)
    c: Horizontal(g669)
    c: Horizontal(g671)
    c: Horizontal(g675)
    c: Vertical(g662)
    c: Vertical(g664)
    c: Vertical(g666)
    c: Vertical(g668)
    c: Vertical(g670)
    c: Vertical(g672)
    c: Vertical(g674)
    c: Vertical(g676)
    c: Horizontal(g677)
    c: Horizontal(g679)
    c: Coincident(g679,g705)
    c: Vertical(g705)
    c: Coincident(g705,g706)
    c: Horizontal(g706)
    c: Coincident(g706,g707)
    c: Coincident(g680,g707)
    c: Horizontal(g680)
    c: Vertical(g707)
    c: Vertical(g691)
    c: Vertical(g693)
    c: Vertical(g689)
    c: Vertical(g685)
    c: Vertical(g683)
    c: Horizontal(g686)
    c: Horizontal(g688)
    c: Horizontal(g690)
    c: Horizontal(g692)
    c: Horizontal(g684)
    c: Vertical(g695)
    c: Coincident(g695,g708)
    c: Coincident(g708,g709)
    c: Coincident(g709,g710)
    c: Coincident(g710,g711)
    c: Coincident(g711,g712)
    c: Coincident(g712,g713)
    c: Horizontal(g713)
    c: Coincident(g713,g714)
    c: Coincident(g714,g715)
    c: Coincident(g715,g716)
    c: Coincident(g716,g717)
    c: Coincident(g718,g719)
    c: Horizontal(g720)
    c: Coincident(g721,g722)
    c: Coincident(g722,g723)
    c: Coincident(g723,g724)
    c: Horizontal(g724)
    c: Coincident(g724,g725)
    c: Horizontal(g726)
    c: Coincident(g726,g727)
    c: Coincident(g727,g728)
    c: Horizontal(g728)
    c: Coincident(g728,g729)
    c: Coincident(g729,g730)
    c: Coincident(g730,g731)
    c: Coincident(g731,g732)
    c: Coincident(g732,g733)
    c: Coincident(g733,g734)
    c: Coincident(g734,g735)
    c: Coincident(g735,g736)
    c: Coincident(g736,g737)
    c: Coincident(g737,g738)
    c: Coincident(g738,g739)
    c: Coincident(g739,g740)
    c: Coincident(g740,g741)
    c: Coincident(g741,g742)
    c: Coincident(g742,g743)
    c: Coincident(g743,g744)
    c: Coincident(g744,g745)
    c: Coincident(g745,g746)
    c: Coincident(g746,g747)
    c: Coincident(g747,g748)
    c: Coincident(g748,g749)
    c: Coincident(g749,g750)
    c: Coincident(g750,g751)
    c: Coincident(g751,g752)
    c: Coincident(g752,g753)
    c: Coincident(g753,g754)
    c: Coincident(g754,g755)
    c: Coincident(g755,g756)
    c: Coincident(g756,g757)
    c: Coincident(g757,g758)
    c: Coincident(g760,g761)
    c: Coincident(g761,g762)
    c: Coincident(g762,g763)
    c: Coincident(g763,g764)
    c: Coincident(g765,g766)
    c: Coincident(g766,g767)
    c: Coincident(g767,g768)
    c: Coincident(g769,g770)
    c: Coincident(g770,g771)
    c: Coincident(g772,g773)
    c: Coincident(g773,g774)
    c: Coincident(g774,g775)
    c: Coincident(g775,g776)
    c: Coincident(g776,g777)
    c: Coincident(g777,g778)
    c: Coincident(g778,g779)
    c: Coincident(g779,g780)
    c: Coincident(g780,g781)
    c: Coincident(g781,g782)
    c: Coincident(g782,g783)
    c: Coincident(g783,g784)
    c: Coincident(g784,g785)
    c: Coincident(g785,g786)
    c: Horizontal(g787)
    c: Coincident(g787,g788)
    c: Coincident(g788,g789)
    c: Coincident(g789,g790)
    c: Coincident(g790,g791)
    c: Horizontal(g791)
    c: Coincident(g791,g792)
    c: Coincident(g792,g793)
    c: Horizontal(g793)
    c: Coincident(g793,g794)
    c: Coincident(g794,g795)
    c: Coincident(g795,g796)
    c: Vertical(g796)
    c: Coincident(g796,g797)
    c: Horizontal(g797)
    c: Coincident(g797,g798)
    c: Coincident(g798,g799)
    c: Horizontal(g799)
    c: Coincident(g799,g800)
    c: Coincident(g800,g801)
    c: Coincident(g801,g802)
    c: Coincident(g802,g803)
    c: Horizontal(g803)
    c: Vertical(g804)
    c: Coincident(g804,g805)
    c: Coincident(g805,g806)
    c: Coincident(g806,g807)
    c: Coincident(g807,g808)
    c: Coincident(g808,g809)
    c: Coincident(g809,g810)
    c: Vertical(g810)
    c: Coincident(g810,g811)
    c: Coincident(g811,g812)
    c: Coincident(g812,g813)
    c: Coincident(g813,g814)
    c: Coincident(g814,g815)
    c: Horizontal(g815)
    c: Coincident(g815,g816)
    c: Coincident(g816,g817)
    c: Coincident(g817,g818)
    c: Coincident(g818,g819)
    c: Coincident(g819,g820)
    c: Coincident(g820,g821)
    c: Horizontal(g821)
    c: Coincident(g821,g822)
    c: Vertical(g822)
    c: Coincident(g822,g823)
    c: Coincident(g823,g824)
    c: Coincident(g824,g825)
    c: Horizontal(g825)
    c: Coincident(g825,g826)
    c: Coincident(g826,g827)
    c: Coincident(g827,g828)
    c: Coincident(g828,g829)
    c: Horizontal(g829)
    c: Coincident(g829,g830)
    c: Coincident(g830,g831)
    c: Coincident(g831,g832)
    c: Coincident(g832,g833)
    c: Horizontal(g834)
    c: Coincident(g834,g835)
    c: Coincident(g835,g836)
    c: Horizontal(g836)
    c: Coincident(g836,g837)
    c: Coincident(g837,g838)
    c: Horizontal(g838)
    c: Coincident(g838,g839)
    c: Coincident(g839,g840)
    c: Coincident(g840,g841)
    c: Coincident(g841,g842)
    c: Coincident(g842,g843)
    c: Coincident(g843,g844)
    c: Coincident(g844,g845)
    c: Coincident(g845,g846)
    c: Coincident(g846,g847)
    c: Coincident(g847,g848)
    c: Horizontal(g848)
    c: Coincident(g848,g849)
    c: Coincident(g849,g850)
    c: Coincident(g850,g851)
    c: Coincident(g851,g852)
    c: Coincident(g852,g853)
    c: Coincident(g853,g854)
    c: Coincident(g854,g855)
    c: Coincident(g855,g856)
    c: Coincident(g856,g857)
    c: Coincident(g857,g858)
    c: Horizontal(g858)
    c: Coincident(g858,g859)
    c: Coincident(g859,g860)
    c: Coincident(g860,g861)
    c: Coincident(g861,g862)
    c: Coincident(g862,g863)
    c: Coincident(g863,g864)
    c: Coincident(g786,g865)
    c: Coincident(g865,g866)
    c: Coincident(g866,g787)
    c: Vertical(g866)
    c: Horizontal(g709)
    c: Horizontal(g711)
    c: Horizontal(g715)
    c: Horizontal(g717)
    c: Horizontal(g719)
    c: Horizontal(g722)
    c: Coincident(g718,g867)
    c: Horizontal(g867)
    c: Coincident(g867,g868)
    c: Coincident(g868,g717)
    c: Coincident(g721,g869)
    c: Coincident(g869,g870)
    c: Coincident(g720,g870)
    c: Coincident(g871,g720)
    c: Coincident(g871,g719)
    c: Vertical(g871)
    c: Vertical(g870)
    c: Vertical(g723)
    c: Horizontal(g869)
    c: Coincident(g872,g726)
    c: Coincident(g873,g872)
    c: Coincident(g725,g873)
    c: Horizontal(g873)
    c: Horizontal(g736)
    c: Horizontal(g734)
    c: Horizontal(g732)
    c: Horizontal(g730)
    c: Horizontal(g738)
    c: Horizontal(g740)
    c: Horizontal(g742)
    c: Horizontal(g744)
    c: Horizontal(g746)
    c: Horizontal(g748)
    c: Horizontal(g750)
    c: Horizontal(g752)
    c: Horizontal(g754)
    c: Coincident(g758,g759)
    c: Horizontal(g756)
    c: Horizontal(g758)
    c: Coincident(g874,g759)
    c: Horizontal(g874)
    c: Coincident(g875,g760)
    c: Coincident(g875,g874)
    c: Horizontal(g760)
    c: Vertical(g762)
    c: Coincident(g765,g764)
    c: Vertical(g764)
    c: Vertical(g766)
    c: Vertical(g768)
    c: Coincident(g769,g768)
    c: Vertical(g770)
    c: Coincident(g876,g771)
    c: Coincident(g877,g772)
    c: Coincident(g877,g876)
    c: Vertical(g772)
    c: Vertical(g774)
    c: Vertical(g776)
    c: Vertical(g778)
    c: Vertical(g780)
    c: Vertical(g782)
    c: Vertical(g876)
    c: Horizontal(g773)
    c: Horizontal(g775)
    c: Horizontal(g777)
    c: Horizontal(g779)
    c: Horizontal(g781)
    c: Horizontal(g783)
    c: Horizontal(g785)
    c: Horizontal(g865)
    c: Vertical(g784)
    c: Vertical(g786)
    c: Vertical(g788)
    c: Vertical(g790)
    c: Horizontal(g789)
    c: Vertical(g792)
    c: Vertical(g794)
    c: Horizontal(g795)
    c: Vertical(g798)
    c: Vertical(g800)
    c: Vertical(g802)
    c: Horizontal(g801)
    c: Coincident(g804,g803)
    c: Horizontal(g805)
    c: Horizontal(g807)
    c: Horizontal(g809)
    c: Vertical(g806)
    c: Vertical(g808)
    c: Vertical(g812)
    c: Vertical(g816)
    c: Vertical(g814)
    c: Vertical(g818)
    c: Vertical(g820)
    c: Vertical(g824)
    c: Vertical(g826)
    c: Vertical(g828)
    c: Vertical(g830)
    c: Vertical(g832)
    c: Horizontal(g827)
    c: Horizontal(g823)
    c: Horizontal(g819)
    c: Horizontal(g817)
    c: Horizontal(g831)
    c: Horizontal(g833)
    c: Coincident(g878,g833)
    c: Coincident(g878,g834)
    c: Vertical(g837)
    c: Horizontal(g840)
    c: Horizontal(g842)
    c: Horizontal(g846)
    c: Horizontal(g850)
    c: Horizontal(g852)
    c: Horizontal(g854)
    c: Horizontal(g856)
    c: Horizontal(g860)
    c: Horizontal(g862)
    c: Horizontal(g864)
    c: Horizontal(g844)
    c: Coincident(g864,g879)
    c: Coincident(g879,g880)
    c: Coincident(g880,g881)
    c: Coincident(g881,g882)
    c: Horizontal(g882)
    c: Coincident(g883,g1)
    c: Coincident(g883,g0)
    c: Vertical(g883)
    c: Coincident(g0,g882)
    c: Coincident(g1,g2)
    c: Coincident(g3,g4)
    c: Coincident(g4,g5)
    c: Coincident(g5,g6)
    c: Coincident(g6,g7)
    c: Coincident(g13,g14)
    c: Coincident(g14,g15)
    c: Coincident(g16,g17)
    c: Coincident(g18,g19)
    c: Coincident(g22,g23)
    c: Coincident(g24,g25)
    c: Coincident(g27,g28)
    c: Vertical(g26)
    c: Coincident(g28,g29)
    c: Coincident(g30,g31)
    c: Horizontal(g29)
    c: Coincident(g37,g38)
    c: Coincident(g38,g39)
    c: Coincident(g39,g40)
    c: Coincident(g40,g41)
    c: Coincident(g42,g43)
    c: Coincident(g20,g21)
    c: Coincident(g21,g22)
    c: Coincident(g25,g26)
    c: Coincident(g48,g49)
    c: Coincident(g49,g50)
    c: Coincident(g58,g59)
    c: Horizontal(g59)
    c: Coincident(g61,g62)
    c: Coincident(g64,g65)
    c: Coincident(g65,g66)
    c: Coincident(g66,g67)
    c: Coincident(g68,g69)
    c: Coincident(g70,g71)
    c: Coincident(g72,g73)
    c: Coincident(g74,g75)
    c: Coincident(g86,g87)
    c: Coincident(g87,g88)
    c: Coincident(g92,g93)
    c: Coincident(g94,g95)
    c: Coincident(g96,g97)
    c: Coincident(g51,g52)
    c: Coincident(g62,g63)
    c: Coincident(g76,g77)
    c: Coincident(g77,g78)
    c: Coincident(g82,g83)
    c: Coincident(g83,g84)
FEATURE [Mesh::Feature] tinker
  Placement = pos=(42,-32.19,20) rot=(1,0,0;1.5708rad)
FEATURE [Part::Extrusion] Extrude
  Base = -> Sketch013
  Dir = (0,1,0)
  DirMode = 0
  FaceMakerClass = Part::FaceMakerBullseye
  FaceMakerMode = 3
  LengthFwd = 10
  LengthRev = 0
  Solid = true
  Symmetric = false
FEATURE [Part::FeaturePython] Clone  label="scaled0_75"  # Draft clone (typed FeaturePython)
  AttacherType = Attacher::AttachEngine3D
  Fuse = false
  Objects = -> [Extrude]
  Scale = (0.75,0.75,0.75)
FEATURE [Part::FeaturePython] Clone001  label="scaled0_85"  # Draft clone (typed FeaturePython)
  AttacherType = Attacher::AttachEngine3D
  Fuse = false
  Objects = -> [Extrude]
  Scale = (0.8,0.8,0.8)
